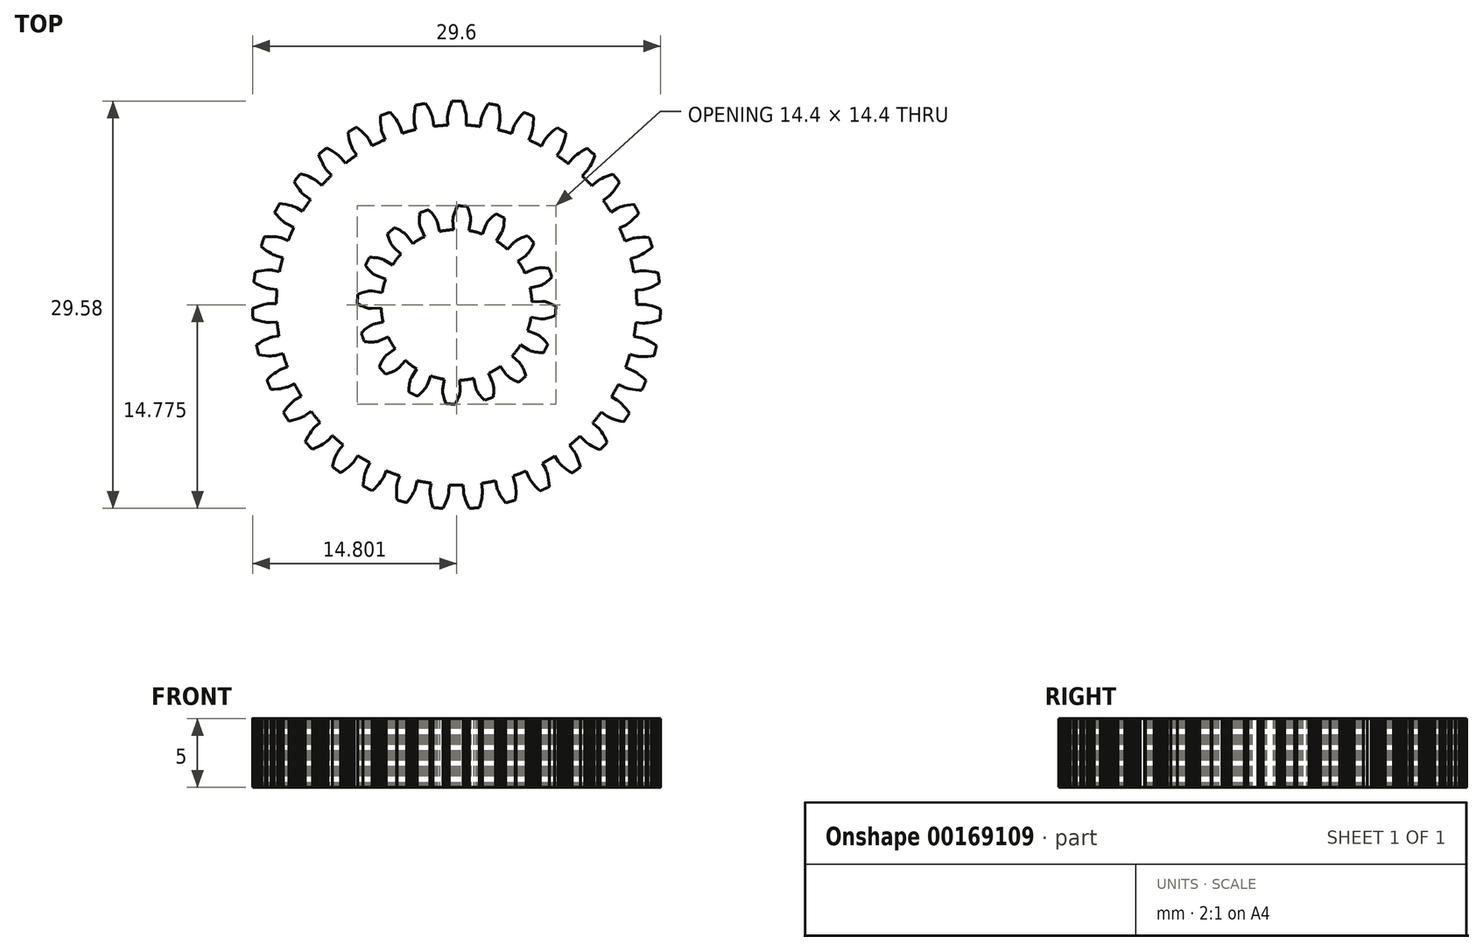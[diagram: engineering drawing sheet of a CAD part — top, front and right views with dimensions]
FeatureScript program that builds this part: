
annotation { "Feature Type Name" : "Feature", "Feature Type Description" : "" }
export const myFeature = defineFeature(function(context is Context, id is Id, definition is map)
    precondition{}
    {
        {
            var Q0;
            Q0=qCreatedBy(makeId("Top.planeOp"),FACE);
            var sketch = newSketch(context, id + "F0", { "sketchPlane" : qUnion([Q0])});
            skLineSegment(sketch, "E0", {"start": v(9.81, 8.62) * mm, "end": v(10.18, 8.94) * mm});
            skLineSegment(sketch, "E1", {"start": v(10.18, 8.94) * mm, "end": v(10.19, 8.95) * mm});
            skLineSegment(sketch, "E2", {"start": v(10.19, 8.95) * mm, "end": v(10.23, 8.98) * mm});
            skLineSegment(sketch, "E3", {"start": v(10.23, 8.98) * mm, "end": v(10.3, 9.03) * mm});
            skLineSegment(sketch, "E4", {"start": v(10.3, 9.03) * mm, "end": v(10.4, 9.1) * mm});
            skLineSegment(sketch, "E5", {"start": v(10.4, 9.1) * mm, "end": v(10.53, 9.16) * mm});
            skLineSegment(sketch, "E6", {"start": v(10.53, 9.16) * mm, "end": v(10.7, 9.24) * mm});
            skLineSegment(sketch, "E7", {"start": v(10.7, 9.24) * mm, "end": v(10.9, 9.33) * mm});
            skLineSegment(sketch, "E8", {"start": v(10.9, 9.33) * mm, "end": v(11.14, 9.41) * mm});
            skLineSegment(sketch, "E9", {"start": v(11.14, 9.41) * mm, "end": v(11.35, 9.48) * mm});
            skArc(sketch, "E10", {"start": v(11.35, 9.48) * mm, "mid": v(11.59, 9.2) * mm, "end": v(11.82, 8.9) * mm});
            skLineSegment(sketch, "E11", {"start": v(11.82, 8.9) * mm, "end": v(11.7, 8.7) * mm});
            skLineSegment(sketch, "E12", {"start": v(11.7, 8.7) * mm, "end": v(11.57, 8.5) * mm});
            skLineSegment(sketch, "E13", {"start": v(11.57, 8.5) * mm, "end": v(11.44, 8.31) * mm});
            skLineSegment(sketch, "E14", {"start": v(11.44, 8.31) * mm, "end": v(11.32, 8.17) * mm});
            skLineSegment(sketch, "E15", {"start": v(11.32, 8.17) * mm, "end": v(11.22, 8.06) * mm});
            skLineSegment(sketch, "E16", {"start": v(11.22, 8.06) * mm, "end": v(11.14, 7.97) * mm});
            skLineSegment(sketch, "E17", {"start": v(11.14, 7.97) * mm, "end": v(11.08, 7.91) * mm});
            skLineSegment(sketch, "E18", {"start": v(11.08, 7.91) * mm, "end": v(11.04, 7.88) * mm});
            skLineSegment(sketch, "E19", {"start": v(11.04, 7.88) * mm, "end": v(11.03, 7.87) * mm});
            skLineSegment(sketch, "E20", {"start": v(11.03, 7.87) * mm, "end": v(10.64, 7.6) * mm});
            skArc(sketch, "E21", {"start": v(10.64, 7.6) * mm, "mid": v(10.93, 7.17) * mm, "end": v(11.2, 6.73) * mm});
            skLineSegment(sketch, "E22", {"start": v(11.2, 6.73) * mm, "end": v(11.61, 6.98) * mm});
            skLineSegment(sketch, "E23", {"start": v(11.61, 6.98) * mm, "end": v(11.63, 6.99) * mm});
            skLineSegment(sketch, "E24", {"start": v(11.63, 6.99) * mm, "end": v(11.67, 7.01) * mm});
            skLineSegment(sketch, "E25", {"start": v(11.67, 7.01) * mm, "end": v(11.75, 7.05) * mm});
            skLineSegment(sketch, "E26", {"start": v(11.75, 7.05) * mm, "end": v(11.86, 7.09) * mm});
            skLineSegment(sketch, "E27", {"start": v(11.86, 7.09) * mm, "end": v(12, 7.13) * mm});
            skLineSegment(sketch, "E28", {"start": v(12, 7.13) * mm, "end": v(12.18, 7.18) * mm});
            skLineSegment(sketch, "E29", {"start": v(12.18, 7.18) * mm, "end": v(12.4, 7.23) * mm});
            skLineSegment(sketch, "E30", {"start": v(12.4, 7.23) * mm, "end": v(12.65, 7.27) * mm});
            skLineSegment(sketch, "E31", {"start": v(12.65, 7.27) * mm, "end": v(12.87, 7.3) * mm});
            skArc(sketch, "E32", {"start": v(12.87, 7.3) * mm, "mid": v(13.05, 6.97) * mm, "end": v(13.22, 6.64) * mm});
            skLineSegment(sketch, "E33", {"start": v(13.22, 6.64) * mm, "end": v(13.08, 6.48) * mm});
            skLineSegment(sketch, "E34", {"start": v(13.08, 6.48) * mm, "end": v(12.9, 6.3) * mm});
            skLineSegment(sketch, "E35", {"start": v(12.9, 6.3) * mm, "end": v(12.74, 6.14) * mm});
            skLineSegment(sketch, "E36", {"start": v(12.74, 6.14) * mm, "end": v(12.6, 6.02) * mm});
            skLineSegment(sketch, "E37", {"start": v(12.6, 6.02) * mm, "end": v(12.48, 5.92) * mm});
            skLineSegment(sketch, "E38", {"start": v(12.48, 5.92) * mm, "end": v(12.39, 5.85) * mm});
            skLineSegment(sketch, "E39", {"start": v(12.39, 5.85) * mm, "end": v(12.32, 5.8) * mm});
            skLineSegment(sketch, "E40", {"start": v(12.32, 5.8) * mm, "end": v(12.27, 5.78) * mm});
            skLineSegment(sketch, "E41", {"start": v(12.27, 5.78) * mm, "end": v(12.26, 5.77) * mm});
            skLineSegment(sketch, "E42", {"start": v(12.26, 5.77) * mm, "end": v(11.82, 5.57) * mm});
            skArc(sketch, "E43", {"start": v(11.82, 5.57) * mm, "mid": v(12.03, 5.1) * mm, "end": v(12.22, 4.62) * mm});
            skLineSegment(sketch, "E44", {"start": v(12.22, 4.62) * mm, "end": v(12.67, 4.8) * mm});
            skLineSegment(sketch, "E45", {"start": v(12.67, 4.8) * mm, "end": v(12.69, 4.8) * mm});
            skLineSegment(sketch, "E46", {"start": v(12.69, 4.8) * mm, "end": v(12.74, 4.81) * mm});
            skLineSegment(sketch, "E47", {"start": v(12.74, 4.81) * mm, "end": v(12.82, 4.83) * mm});
            skLineSegment(sketch, "E48", {"start": v(12.82, 4.83) * mm, "end": v(12.94, 4.86) * mm});
            skLineSegment(sketch, "E49", {"start": v(12.94, 4.86) * mm, "end": v(13.09, 4.88) * mm});
            skLineSegment(sketch, "E50", {"start": v(13.09, 4.88) * mm, "end": v(13.27, 4.9) * mm});
            skLineSegment(sketch, "E51", {"start": v(13.27, 4.9) * mm, "end": v(13.5, 4.9) * mm});
            skLineSegment(sketch, "E52", {"start": v(13.5, 4.9) * mm, "end": v(13.75, 4.9) * mm});
            skLineSegment(sketch, "E53", {"start": v(13.75, 4.9) * mm, "end": v(13.97, 4.88) * mm});
            skArc(sketch, "E54", {"start": v(13.97, 4.88) * mm, "mid": v(14.09, 4.53) * mm, "end": v(14.2, 4.18) * mm});
            skLineSegment(sketch, "E55", {"start": v(14.2, 4.18) * mm, "end": v(14.03, 4.04) * mm});
            skLineSegment(sketch, "E56", {"start": v(14.03, 4.04) * mm, "end": v(13.82, 3.89) * mm});
            skLineSegment(sketch, "E57", {"start": v(13.82, 3.89) * mm, "end": v(13.64, 3.76) * mm});
            skLineSegment(sketch, "E58", {"start": v(13.64, 3.76) * mm, "end": v(13.48, 3.67) * mm});
            skLineSegment(sketch, "E59", {"start": v(13.48, 3.67) * mm, "end": v(13.34, 3.6) * mm});
            skLineSegment(sketch, "E60", {"start": v(13.34, 3.6) * mm, "end": v(13.24, 3.55) * mm});
            skLineSegment(sketch, "E61", {"start": v(13.24, 3.55) * mm, "end": v(13.16, 3.51) * mm});
            skLineSegment(sketch, "E62", {"start": v(13.16, 3.51) * mm, "end": v(13.1, 3.5) * mm});
            skLineSegment(sketch, "E63", {"start": v(13.1, 3.5) * mm, "end": v(13.1, 3.5) * mm});
            skLineSegment(sketch, "E64", {"start": v(13.1, 3.5) * mm, "end": v(12.63, 3.37) * mm});
            skArc(sketch, "E65", {"start": v(12.63, 3.37) * mm, "mid": v(12.75, 2.87) * mm, "end": v(12.86, 2.37) * mm});
            skLineSegment(sketch, "E66", {"start": v(12.86, 2.37) * mm, "end": v(13.33, 2.45) * mm});
            skLineSegment(sketch, "E67", {"start": v(13.33, 2.45) * mm, "end": v(13.34, 2.46) * mm});
            skLineSegment(sketch, "E68", {"start": v(13.34, 2.46) * mm, "end": v(13.4, 2.46) * mm});
            skLineSegment(sketch, "E69", {"start": v(13.4, 2.46) * mm, "end": v(13.48, 2.47) * mm});
            skLineSegment(sketch, "E70", {"start": v(13.48, 2.47) * mm, "end": v(13.6, 2.47) * mm});
            skLineSegment(sketch, "E71", {"start": v(13.6, 2.47) * mm, "end": v(13.75, 2.46) * mm});
            skLineSegment(sketch, "E72", {"start": v(13.75, 2.46) * mm, "end": v(13.94, 2.44) * mm});
            skLineSegment(sketch, "E73", {"start": v(13.94, 2.44) * mm, "end": v(14.15, 2.41) * mm});
            skLineSegment(sketch, "E74", {"start": v(14.15, 2.41) * mm, "end": v(14.4, 2.36) * mm});
            skLineSegment(sketch, "E75", {"start": v(14.4, 2.36) * mm, "end": v(14.62, 2.31) * mm});
            skArc(sketch, "E76", {"start": v(14.62, 2.31) * mm, "mid": v(14.67, 1.94) * mm, "end": v(14.71, 1.57) * mm});
            skLineSegment(sketch, "E77", {"start": v(14.71, 1.57) * mm, "end": v(14.52, 1.47) * mm});
            skLineSegment(sketch, "E78", {"start": v(14.52, 1.47) * mm, "end": v(14.3, 1.36) * mm});
            skLineSegment(sketch, "E79", {"start": v(14.3, 1.36) * mm, "end": v(14.1, 1.27) * mm});
            skLineSegment(sketch, "E80", {"start": v(14.1, 1.27) * mm, "end": v(13.92, 1.2) * mm});
            skLineSegment(sketch, "E81", {"start": v(13.92, 1.2) * mm, "end": v(13.77, 1.16) * mm});
            skLineSegment(sketch, "E82", {"start": v(13.77, 1.16) * mm, "end": v(13.66, 1.13) * mm});
            skLineSegment(sketch, "E83", {"start": v(13.66, 1.13) * mm, "end": v(13.58, 1.1) * mm});
            skLineSegment(sketch, "E84", {"start": v(13.58, 1.1) * mm, "end": v(13.53, 1.1) * mm});
            skLineSegment(sketch, "E85", {"start": v(13.53, 1.1) * mm, "end": v(13.5, 1.1) * mm});
            skLineSegment(sketch, "E86", {"start": v(13.5, 1.1) * mm, "end": v(13.03, 1.06) * mm});
            skArc(sketch, "E87", {"start": v(13.03, 1.06) * mm, "mid": v(13.06, 0.55) * mm, "end": v(13.07, 0.03) * mm});
            skLineSegment(sketch, "E88", {"start": v(13.07, 0.03) * mm, "end": v(13.55, 0.04) * mm});
            skLineSegment(sketch, "E89", {"start": v(13.55, 0.04) * mm, "end": v(13.57, 0.03) * mm});
            skLineSegment(sketch, "E90", {"start": v(13.57, 0.03) * mm, "end": v(13.62, 0.03) * mm});
            skLineSegment(sketch, "E91", {"start": v(13.62, 0.03) * mm, "end": v(13.7, 0.02) * mm});
            skLineSegment(sketch, "E92", {"start": v(13.7, 0.02) * mm, "end": v(13.82, 0) * mm});
            skLineSegment(sketch, "E93", {"start": v(13.82, 0) * mm, "end": v(13.97, -0.03) * mm});
            skLineSegment(sketch, "E94", {"start": v(13.97, -0.03) * mm, "end": v(14.15, -0.08) * mm});
            skLineSegment(sketch, "E95", {"start": v(14.15, -0.08) * mm, "end": v(14.36, -0.15) * mm});
            skLineSegment(sketch, "E96", {"start": v(14.36, -0.15) * mm, "end": v(14.6, -0.25) * mm});
            skLineSegment(sketch, "E97", {"start": v(14.6, -0.25) * mm, "end": v(14.8, -0.34) * mm});
            skArc(sketch, "E98", {"start": v(14.8, -0.34) * mm, "mid": v(14.78, -0.7) * mm, "end": v(14.76, -1.08) * mm});
            skLineSegment(sketch, "E99", {"start": v(14.76, -1.08) * mm, "end": v(14.55, -1.15) * mm});
            skLineSegment(sketch, "E100", {"start": v(14.55, -1.15) * mm, "end": v(14.31, -1.22) * mm});
            skLineSegment(sketch, "E101", {"start": v(14.31, -1.22) * mm, "end": v(14.1, -1.27) * mm});
            skLineSegment(sketch, "E102", {"start": v(14.1, -1.27) * mm, "end": v(13.91, -1.3) * mm});
            skLineSegment(sketch, "E103", {"start": v(13.91, -1.3) * mm, "end": v(13.76, -1.32) * mm});
            skLineSegment(sketch, "E104", {"start": v(13.76, -1.32) * mm, "end": v(13.64, -1.33) * mm});
            skLineSegment(sketch, "E105", {"start": v(13.64, -1.33) * mm, "end": v(13.56, -1.33) * mm});
            skLineSegment(sketch, "E106", {"start": v(13.56, -1.33) * mm, "end": v(13.5, -1.33) * mm});
            skLineSegment(sketch, "E107", {"start": v(13.5, -1.33) * mm, "end": v(13.5, -1.33) * mm});
            skLineSegment(sketch, "E108", {"start": v(13.5, -1.33) * mm, "end": v(13.01, -1.28) * mm});
            skArc(sketch, "E109", {"start": v(13.01, -1.28) * mm, "mid": v(12.95, -1.8) * mm, "end": v(12.87, -2.3) * mm});
            skLineSegment(sketch, "E110", {"start": v(12.87, -2.3) * mm, "end": v(13.35, -2.39) * mm});
            skLineSegment(sketch, "E111", {"start": v(13.35, -2.39) * mm, "end": v(13.36, -2.39) * mm});
            skLineSegment(sketch, "E112", {"start": v(13.36, -2.39) * mm, "end": v(13.41, -2.4) * mm});
            skLineSegment(sketch, "E113", {"start": v(13.41, -2.4) * mm, "end": v(13.5, -2.43) * mm});
            skLineSegment(sketch, "E114", {"start": v(13.5, -2.43) * mm, "end": v(13.6, -2.47) * mm});
            skLineSegment(sketch, "E115", {"start": v(13.6, -2.47) * mm, "end": v(13.74, -2.53) * mm});
            skLineSegment(sketch, "E116", {"start": v(13.74, -2.53) * mm, "end": v(13.91, -2.6) * mm});
            skLineSegment(sketch, "E117", {"start": v(13.91, -2.6) * mm, "end": v(14.1, -2.72) * mm});
            skLineSegment(sketch, "E118", {"start": v(14.1, -2.72) * mm, "end": v(14.32, -2.85) * mm});
            skLineSegment(sketch, "E119", {"start": v(14.32, -2.85) * mm, "end": v(14.5, -2.97) * mm});
            skArc(sketch, "E120", {"start": v(14.5, -2.97) * mm, "mid": v(14.42, -3.34) * mm, "end": v(14.34, -3.7) * mm});
            skLineSegment(sketch, "E121", {"start": v(14.34, -3.7) * mm, "end": v(14.12, -3.73) * mm});
            skLineSegment(sketch, "E122", {"start": v(14.12, -3.73) * mm, "end": v(13.87, -3.75) * mm});
            skLineSegment(sketch, "E123", {"start": v(13.87, -3.75) * mm, "end": v(13.65, -3.77) * mm});
            skLineSegment(sketch, "E124", {"start": v(13.65, -3.77) * mm, "end": v(13.46, -3.77) * mm});
            skLineSegment(sketch, "E125", {"start": v(13.46, -3.77) * mm, "end": v(13.3, -3.76) * mm});
            skLineSegment(sketch, "E126", {"start": v(13.3, -3.76) * mm, "end": v(13.19, -3.75) * mm});
            skLineSegment(sketch, "E127", {"start": v(13.19, -3.75) * mm, "end": v(13.1, -3.73) * mm});
            skLineSegment(sketch, "E128", {"start": v(13.1, -3.73) * mm, "end": v(13.06, -3.72) * mm});
            skLineSegment(sketch, "E129", {"start": v(13.06, -3.72) * mm, "end": v(13.04, -3.72) * mm});
            skLineSegment(sketch, "E130", {"start": v(13.04, -3.72) * mm, "end": v(12.58, -3.59) * mm});
            skArc(sketch, "E131", {"start": v(12.58, -3.59) * mm, "mid": v(12.43, -4.08) * mm, "end": v(12.26, -4.56) * mm});
            skLineSegment(sketch, "E132", {"start": v(12.26, -4.56) * mm, "end": v(12.7, -4.73) * mm});
            skLineSegment(sketch, "E133", {"start": v(12.7, -4.73) * mm, "end": v(12.72, -4.74) * mm});
            skLineSegment(sketch, "E134", {"start": v(12.72, -4.74) * mm, "end": v(12.77, -4.76) * mm});
            skLineSegment(sketch, "E135", {"start": v(12.77, -4.76) * mm, "end": v(12.84, -4.8) * mm});
            skLineSegment(sketch, "E136", {"start": v(12.84, -4.8) * mm, "end": v(12.95, -4.86) * mm});
            skLineSegment(sketch, "E137", {"start": v(12.95, -4.86) * mm, "end": v(13.07, -4.94) * mm});
            skLineSegment(sketch, "E138", {"start": v(13.07, -4.94) * mm, "end": v(13.22, -5.05) * mm});
            skLineSegment(sketch, "E139", {"start": v(13.22, -5.05) * mm, "end": v(13.4, -5.2) * mm});
            skLineSegment(sketch, "E140", {"start": v(13.4, -5.2) * mm, "end": v(13.58, -5.36) * mm});
            skLineSegment(sketch, "E141", {"start": v(13.58, -5.36) * mm, "end": v(13.74, -5.51) * mm});
            skArc(sketch, "E142", {"start": v(13.74, -5.51) * mm, "mid": v(13.6, -5.86) * mm, "end": v(13.45, -6.2) * mm});
            skLineSegment(sketch, "E143", {"start": v(13.45, -6.2) * mm, "end": v(13.23, -6.2) * mm});
            skLineSegment(sketch, "E144", {"start": v(13.23, -6.2) * mm, "end": v(12.97, -6.17) * mm});
            skLineSegment(sketch, "E145", {"start": v(12.97, -6.17) * mm, "end": v(12.76, -6.14) * mm});
            skLineSegment(sketch, "E146", {"start": v(12.76, -6.14) * mm, "end": v(12.57, -6.1) * mm});
            skLineSegment(sketch, "E147", {"start": v(12.57, -6.1) * mm, "end": v(12.42, -6.07) * mm});
            skLineSegment(sketch, "E148", {"start": v(12.42, -6.07) * mm, "end": v(12.31, -6.04) * mm});
            skLineSegment(sketch, "E149", {"start": v(12.31, -6.04) * mm, "end": v(12.23, -6.01) * mm});
            skLineSegment(sketch, "E150", {"start": v(12.23, -6.01) * mm, "end": v(12.18, -6) * mm});
            skLineSegment(sketch, "E151", {"start": v(12.18, -6) * mm, "end": v(12.17, -5.99) * mm});
            skLineSegment(sketch, "E152", {"start": v(12.17, -5.99) * mm, "end": v(11.74, -5.78) * mm});
            skArc(sketch, "E153", {"start": v(11.74, -5.78) * mm, "mid": v(11.5, -6.23) * mm, "end": v(11.25, -6.68) * mm});
            skLineSegment(sketch, "E154", {"start": v(11.25, -6.68) * mm, "end": v(11.66, -6.92) * mm});
            skLineSegment(sketch, "E155", {"start": v(11.66, -6.92) * mm, "end": v(11.68, -6.93) * mm});
            skLineSegment(sketch, "E156", {"start": v(11.68, -6.93) * mm, "end": v(11.72, -6.96) * mm});
            skLineSegment(sketch, "E157", {"start": v(11.72, -6.96) * mm, "end": v(11.78, -7.01) * mm});
            skLineSegment(sketch, "E158", {"start": v(11.78, -7.01) * mm, "end": v(11.87, -7.1) * mm});
            skLineSegment(sketch, "E159", {"start": v(11.87, -7.1) * mm, "end": v(11.98, -7.2) * mm});
            skLineSegment(sketch, "E160", {"start": v(11.98, -7.2) * mm, "end": v(12.11, -7.33) * mm});
            skLineSegment(sketch, "E161", {"start": v(12.11, -7.33) * mm, "end": v(12.26, -7.5) * mm});
            skLineSegment(sketch, "E162", {"start": v(12.26, -7.5) * mm, "end": v(12.41, -7.7) * mm});
            skLineSegment(sketch, "E163", {"start": v(12.41, -7.7) * mm, "end": v(12.54, -7.88) * mm});
            skArc(sketch, "E164", {"start": v(12.54, -7.88) * mm, "mid": v(12.34, -8.2) * mm, "end": v(12.13, -8.5) * mm});
            skLineSegment(sketch, "E165", {"start": v(12.13, -8.5) * mm, "end": v(11.91, -8.45) * mm});
            skLineSegment(sketch, "E166", {"start": v(11.91, -8.45) * mm, "end": v(11.67, -8.39) * mm});
            skLineSegment(sketch, "E167", {"start": v(11.67, -8.39) * mm, "end": v(11.46, -8.32) * mm});
            skLineSegment(sketch, "E168", {"start": v(11.46, -8.32) * mm, "end": v(11.28, -8.25) * mm});
            skLineSegment(sketch, "E169", {"start": v(11.28, -8.25) * mm, "end": v(11.14, -8.2) * mm});
            skLineSegment(sketch, "E170", {"start": v(11.14, -8.2) * mm, "end": v(11.04, -8.14) * mm});
            skLineSegment(sketch, "E171", {"start": v(11.04, -8.14) * mm, "end": v(10.96, -8.1) * mm});
            skLineSegment(sketch, "E172", {"start": v(10.96, -8.1) * mm, "end": v(10.92, -8.07) * mm});
            skLineSegment(sketch, "E173", {"start": v(10.92, -8.07) * mm, "end": v(10.9, -8.06) * mm});
            skLineSegment(sketch, "E174", {"start": v(10.9, -8.06) * mm, "end": v(10.52, -7.78) * mm});
            skArc(sketch, "E175", {"start": v(10.52, -7.78) * mm, "mid": v(10.2, -8.19) * mm, "end": v(9.88, -8.58) * mm});
            skLineSegment(sketch, "E176", {"start": v(9.88, -8.58) * mm, "end": v(10.24, -8.9) * mm});
            skLineSegment(sketch, "E177", {"start": v(10.24, -8.9) * mm, "end": v(10.25, -8.9) * mm});
            skLineSegment(sketch, "E178", {"start": v(10.25, -8.9) * mm, "end": v(10.29, -8.94) * mm});
            skLineSegment(sketch, "E179", {"start": v(10.29, -8.94) * mm, "end": v(10.34, -9) * mm});
            skLineSegment(sketch, "E180", {"start": v(10.34, -9) * mm, "end": v(10.42, -9.1) * mm});
            skLineSegment(sketch, "E181", {"start": v(10.42, -9.1) * mm, "end": v(10.5, -9.22) * mm});
            skLineSegment(sketch, "E182", {"start": v(10.5, -9.22) * mm, "end": v(10.61, -9.38) * mm});
            skLineSegment(sketch, "E183", {"start": v(10.61, -9.38) * mm, "end": v(10.72, -9.57) * mm});
            skLineSegment(sketch, "E184", {"start": v(10.72, -9.57) * mm, "end": v(10.84, -9.8) * mm});
            skLineSegment(sketch, "E185", {"start": v(10.84, -9.8) * mm, "end": v(10.93, -10) * mm});
            skArc(sketch, "E186", {"start": v(10.93, -10) * mm, "mid": v(10.68, -10.26) * mm, "end": v(10.42, -10.53) * mm});
            skLineSegment(sketch, "E187", {"start": v(10.42, -10.53) * mm, "end": v(10.21, -10.44) * mm});
            skLineSegment(sketch, "E188", {"start": v(10.21, -10.44) * mm, "end": v(9.98, -10.34) * mm});
            skLineSegment(sketch, "E189", {"start": v(9.98, -10.34) * mm, "end": v(9.8, -10.23) * mm});
            skLineSegment(sketch, "E190", {"start": v(9.8, -10.23) * mm, "end": v(9.63, -10.14) * mm});
            skLineSegment(sketch, "E191", {"start": v(9.63, -10.14) * mm, "end": v(9.5, -10.05) * mm});
            skLineSegment(sketch, "E192", {"start": v(9.5, -10.05) * mm, "end": v(9.4, -9.98) * mm});
            skLineSegment(sketch, "E193", {"start": v(9.4, -9.98) * mm, "end": v(9.34, -9.93) * mm});
            skLineSegment(sketch, "E194", {"start": v(9.34, -9.93) * mm, "end": v(9.3, -9.9) * mm});
            skLineSegment(sketch, "E195", {"start": v(9.3, -9.9) * mm, "end": v(9.3, -9.88) * mm});
            skLineSegment(sketch, "E196", {"start": v(9.3, -9.88) * mm, "end": v(8.96, -9.53) * mm});
            skArc(sketch, "E197", {"start": v(8.96, -9.53) * mm, "mid": v(8.58, -9.88) * mm, "end": v(8.19, -10.2) * mm});
            skLineSegment(sketch, "E198", {"start": v(8.19, -10.2) * mm, "end": v(8.5, -10.58) * mm});
            skLineSegment(sketch, "E199", {"start": v(8.5, -10.58) * mm, "end": v(8.5, -10.6) * mm});
            skLineSegment(sketch, "E200", {"start": v(8.5, -10.6) * mm, "end": v(8.53, -10.64) * mm});
            skLineSegment(sketch, "E201", {"start": v(8.53, -10.64) * mm, "end": v(8.57, -10.7) * mm});
            skLineSegment(sketch, "E202", {"start": v(8.57, -10.7) * mm, "end": v(8.63, -10.81) * mm});
            skLineSegment(sketch, "E203", {"start": v(8.63, -10.81) * mm, "end": v(8.7, -10.95) * mm});
            skLineSegment(sketch, "E204", {"start": v(8.7, -10.95) * mm, "end": v(8.77, -11.12) * mm});
            skLineSegment(sketch, "E205", {"start": v(8.77, -11.12) * mm, "end": v(8.85, -11.33) * mm});
            skLineSegment(sketch, "E206", {"start": v(8.85, -11.33) * mm, "end": v(8.92, -11.57) * mm});
            skLineSegment(sketch, "E207", {"start": v(8.92, -11.57) * mm, "end": v(8.98, -11.78) * mm});
            skArc(sketch, "E208", {"start": v(8.98, -11.78) * mm, "mid": v(8.68, -12) * mm, "end": v(8.37, -12.22) * mm});
            skLineSegment(sketch, "E209", {"start": v(8.37, -12.22) * mm, "end": v(8.19, -12.1) * mm});
            skLineSegment(sketch, "E210", {"start": v(8.19, -12.1) * mm, "end": v(7.98, -11.95) * mm});
            skLineSegment(sketch, "E211", {"start": v(7.98, -11.95) * mm, "end": v(7.8, -11.82) * mm});
            skLineSegment(sketch, "E212", {"start": v(7.8, -11.82) * mm, "end": v(7.67, -11.7) * mm});
            skLineSegment(sketch, "E213", {"start": v(7.67, -11.7) * mm, "end": v(7.56, -11.59) * mm});
            skLineSegment(sketch, "E214", {"start": v(7.56, -11.59) * mm, "end": v(7.48, -11.5) * mm});
            skLineSegment(sketch, "E215", {"start": v(7.48, -11.5) * mm, "end": v(7.42, -11.44) * mm});
            skLineSegment(sketch, "E216", {"start": v(7.42, -11.44) * mm, "end": v(7.4, -11.4) * mm});
            skLineSegment(sketch, "E217", {"start": v(7.4, -11.4) * mm, "end": v(7.38, -11.38) * mm});
            skLineSegment(sketch, "E218", {"start": v(7.38, -11.38) * mm, "end": v(7.12, -10.98) * mm});
            skArc(sketch, "E219", {"start": v(7.12, -10.98) * mm, "mid": v(6.68, -11.25) * mm, "end": v(6.24, -11.5) * mm});
            skLineSegment(sketch, "E220", {"start": v(6.24, -11.5) * mm, "end": v(6.47, -11.93) * mm});
            skLineSegment(sketch, "E221", {"start": v(6.47, -11.93) * mm, "end": v(6.47, -11.94) * mm});
            skLineSegment(sketch, "E222", {"start": v(6.47, -11.94) * mm, "end": v(6.5, -11.99) * mm});
            skLineSegment(sketch, "E223", {"start": v(6.5, -11.99) * mm, "end": v(6.53, -12.07) * mm});
            skLineSegment(sketch, "E224", {"start": v(6.53, -12.07) * mm, "end": v(6.56, -12.18) * mm});
            skLineSegment(sketch, "E225", {"start": v(6.56, -12.18) * mm, "end": v(6.6, -12.33) * mm});
            skLineSegment(sketch, "E226", {"start": v(6.6, -12.33) * mm, "end": v(6.65, -12.5) * mm});
            skLineSegment(sketch, "E227", {"start": v(6.65, -12.5) * mm, "end": v(6.68, -12.73) * mm});
            skLineSegment(sketch, "E228", {"start": v(6.68, -12.73) * mm, "end": v(6.71, -12.98) * mm});
            skLineSegment(sketch, "E229", {"start": v(6.71, -12.98) * mm, "end": v(6.73, -13.2) * mm});
            skArc(sketch, "E230", {"start": v(6.73, -13.2) * mm, "mid": v(6.4, -13.36) * mm, "end": v(6.06, -13.52) * mm});
            skLineSegment(sketch, "E231", {"start": v(6.06, -13.52) * mm, "end": v(5.9, -13.37) * mm});
            skLineSegment(sketch, "E232", {"start": v(5.9, -13.37) * mm, "end": v(5.72, -13.19) * mm});
            skLineSegment(sketch, "E233", {"start": v(5.72, -13.19) * mm, "end": v(5.58, -13.02) * mm});
            skLineSegment(sketch, "E234", {"start": v(5.58, -13.02) * mm, "end": v(5.46, -12.88) * mm});
            skLineSegment(sketch, "E235", {"start": v(5.46, -12.88) * mm, "end": v(5.37, -12.75) * mm});
            skLineSegment(sketch, "E236", {"start": v(5.37, -12.75) * mm, "end": v(5.3, -12.65) * mm});
            skLineSegment(sketch, "E237", {"start": v(5.3, -12.65) * mm, "end": v(5.26, -12.58) * mm});
            skLineSegment(sketch, "E238", {"start": v(5.26, -12.58) * mm, "end": v(5.24, -12.53) * mm});
            skLineSegment(sketch, "E239", {"start": v(5.24, -12.53) * mm, "end": v(5.23, -12.52) * mm});
            skLineSegment(sketch, "E240", {"start": v(5.23, -12.52) * mm, "end": v(5.05, -12.08) * mm});
            skArc(sketch, "E241", {"start": v(5.05, -12.08) * mm, "mid": v(4.57, -12.26) * mm, "end": v(4.09, -12.43) * mm});
            skLineSegment(sketch, "E242", {"start": v(4.09, -12.43) * mm, "end": v(4.24, -12.89) * mm});
            skLineSegment(sketch, "E243", {"start": v(4.24, -12.89) * mm, "end": v(4.24, -12.9) * mm});
            skLineSegment(sketch, "E244", {"start": v(4.24, -12.9) * mm, "end": v(4.25, -12.96) * mm});
            skLineSegment(sketch, "E245", {"start": v(4.25, -12.96) * mm, "end": v(4.27, -13.04) * mm});
            skLineSegment(sketch, "E246", {"start": v(4.27, -13.04) * mm, "end": v(4.29, -13.16) * mm});
            skLineSegment(sketch, "E247", {"start": v(4.29, -13.16) * mm, "end": v(4.3, -13.3) * mm});
            skLineSegment(sketch, "E248", {"start": v(4.3, -13.3) * mm, "end": v(4.3, -13.5) * mm});
            skLineSegment(sketch, "E249", {"start": v(4.3, -13.5) * mm, "end": v(4.3, -13.71) * mm});
            skLineSegment(sketch, "E250", {"start": v(4.3, -13.71) * mm, "end": v(4.3, -13.97) * mm});
            skLineSegment(sketch, "E251", {"start": v(4.3, -13.97) * mm, "end": v(4.27, -14.19) * mm});
            skArc(sketch, "E252", {"start": v(4.27, -14.19) * mm, "mid": v(3.91, -14.29) * mm, "end": v(3.55, -14.38) * mm});
            skLineSegment(sketch, "E253", {"start": v(3.55, -14.38) * mm, "end": v(3.42, -14.2) * mm});
            skLineSegment(sketch, "E254", {"start": v(3.42, -14.2) * mm, "end": v(3.28, -14) * mm});
            skLineSegment(sketch, "E255", {"start": v(3.28, -14) * mm, "end": v(3.16, -13.8) * mm});
            skLineSegment(sketch, "E256", {"start": v(3.16, -13.8) * mm, "end": v(3.08, -13.64) * mm});
            skLineSegment(sketch, "E257", {"start": v(3.08, -13.64) * mm, "end": v(3.01, -13.5) * mm});
            skLineSegment(sketch, "E258", {"start": v(3.01, -13.5) * mm, "end": v(2.96, -13.4) * mm});
            skLineSegment(sketch, "E259", {"start": v(2.96, -13.4) * mm, "end": v(2.94, -13.32) * mm});
            skLineSegment(sketch, "E260", {"start": v(2.94, -13.32) * mm, "end": v(2.92, -13.27) * mm});
            skLineSegment(sketch, "E261", {"start": v(2.92, -13.27) * mm, "end": v(2.92, -13.25) * mm});
            skLineSegment(sketch, "E262", {"start": v(2.92, -13.25) * mm, "end": v(2.81, -12.78) * mm});
            skArc(sketch, "E263", {"start": v(2.81, -12.78) * mm, "mid": v(2.31, -12.88) * mm, "end": v(1.8, -12.96) * mm});
            skLineSegment(sketch, "E264", {"start": v(1.8, -12.96) * mm, "end": v(1.87, -13.44) * mm});
            skLineSegment(sketch, "E265", {"start": v(1.87, -13.44) * mm, "end": v(1.87, -13.46) * mm});
            skLineSegment(sketch, "E266", {"start": v(1.87, -13.46) * mm, "end": v(1.87, -13.5) * mm});
            skLineSegment(sketch, "E267", {"start": v(1.87, -13.5) * mm, "end": v(1.87, -13.6) * mm});
            skLineSegment(sketch, "E268", {"start": v(1.87, -13.6) * mm, "end": v(1.87, -13.7) * mm});
            skLineSegment(sketch, "E269", {"start": v(1.87, -13.7) * mm, "end": v(1.86, -13.86) * mm});
            skLineSegment(sketch, "E270", {"start": v(1.86, -13.86) * mm, "end": v(1.83, -14.05) * mm});
            skLineSegment(sketch, "E271", {"start": v(1.83, -14.05) * mm, "end": v(1.8, -14.26) * mm});
            skLineSegment(sketch, "E272", {"start": v(1.8, -14.26) * mm, "end": v(1.73, -14.5) * mm});
            skLineSegment(sketch, "E273", {"start": v(1.73, -14.5) * mm, "end": v(1.67, -14.72) * mm});
            skArc(sketch, "E274", {"start": v(1.67, -14.72) * mm, "mid": v(1.3, -14.76) * mm, "end": v(0.93, -14.79) * mm});
            skLineSegment(sketch, "E275", {"start": v(0.93, -14.79) * mm, "end": v(0.83, -14.59) * mm});
            skLineSegment(sketch, "E276", {"start": v(0.83, -14.59) * mm, "end": v(0.73, -14.36) * mm});
            skLineSegment(sketch, "E277", {"start": v(0.73, -14.36) * mm, "end": v(0.65, -14.15) * mm});
            skLineSegment(sketch, "E278", {"start": v(0.65, -14.15) * mm, "end": v(0.6, -13.97) * mm});
            skLineSegment(sketch, "E279", {"start": v(0.6, -13.97) * mm, "end": v(0.55, -13.83) * mm});
            skLineSegment(sketch, "E280", {"start": v(0.55, -13.83) * mm, "end": v(0.53, -13.71) * mm});
            skLineSegment(sketch, "E281", {"start": v(0.53, -13.71) * mm, "end": v(0.51, -13.63) * mm});
            skLineSegment(sketch, "E282", {"start": v(0.51, -13.63) * mm, "end": v(0.5, -13.58) * mm});
            skLineSegment(sketch, "E283", {"start": v(0.5, -13.58) * mm, "end": v(0.5, -13.56) * mm});
            skLineSegment(sketch, "E284", {"start": v(0.5, -13.56) * mm, "end": v(0.49, -13.08) * mm});
            skArc(sketch, "E285", {"start": v(0.49, -13.08) * mm, "mid": v(-0.02, -13.09) * mm, "end": v(-0.54, -13.08) * mm});
            skLineSegment(sketch, "E286", {"start": v(-0.54, -13.08) * mm, "end": v(-0.56, -13.56) * mm});
            skLineSegment(sketch, "E287", {"start": v(-0.56, -13.56) * mm, "end": v(-0.56, -13.57) * mm});
            skLineSegment(sketch, "E288", {"start": v(-0.56, -13.57) * mm, "end": v(-0.57, -13.62) * mm});
            skLineSegment(sketch, "E289", {"start": v(-0.57, -13.62) * mm, "end": v(-0.58, -13.7) * mm});
            skLineSegment(sketch, "E290", {"start": v(-0.58, -13.7) * mm, "end": v(-0.6, -13.82) * mm});
            skLineSegment(sketch, "E291", {"start": v(-0.6, -13.82) * mm, "end": v(-0.65, -13.97) * mm});
            skLineSegment(sketch, "E292", {"start": v(-0.65, -13.97) * mm, "end": v(-0.7, -14.15) * mm});
            skLineSegment(sketch, "E293", {"start": v(-0.7, -14.15) * mm, "end": v(-0.78, -14.35) * mm});
            skLineSegment(sketch, "E294", {"start": v(-0.78, -14.35) * mm, "end": v(-0.89, -14.59) * mm});
            skLineSegment(sketch, "E295", {"start": v(-0.89, -14.59) * mm, "end": v(-0.98, -14.78) * mm});
            skArc(sketch, "E296", {"start": v(-0.98, -14.78) * mm, "mid": v(-1.35, -14.75) * mm, "end": v(-1.72, -14.71) * mm});
            skLineSegment(sketch, "E297", {"start": v(-1.72, -14.71) * mm, "end": v(-1.79, -14.5) * mm});
            skLineSegment(sketch, "E298", {"start": v(-1.79, -14.5) * mm, "end": v(-1.84, -14.26) * mm});
            skLineSegment(sketch, "E299", {"start": v(-1.84, -14.26) * mm, "end": v(-1.88, -14.04) * mm});
            skLineSegment(sketch, "E300", {"start": v(-1.88, -14.04) * mm, "end": v(-1.9, -13.85) * mm});
            skLineSegment(sketch, "E301", {"start": v(-1.9, -13.85) * mm, "end": v(-1.92, -13.7) * mm});
            skLineSegment(sketch, "E302", {"start": v(-1.92, -13.7) * mm, "end": v(-1.93, -13.58) * mm});
            skLineSegment(sketch, "E303", {"start": v(-1.93, -13.58) * mm, "end": v(-1.92, -13.5) * mm});
            skLineSegment(sketch, "E304", {"start": v(-1.92, -13.5) * mm, "end": v(-1.92, -13.45) * mm});
            skLineSegment(sketch, "E305", {"start": v(-1.92, -13.45) * mm, "end": v(-1.92, -13.43) * mm});
            skLineSegment(sketch, "E306", {"start": v(-1.92, -13.43) * mm, "end": v(-1.85, -12.96) * mm});
            skArc(sketch, "E307", {"start": v(-1.85, -12.96) * mm, "mid": v(-2.36, -12.87) * mm, "end": v(-2.86, -12.77) * mm});
            skLineSegment(sketch, "E308", {"start": v(-2.86, -12.77) * mm, "end": v(-2.97, -13.24) * mm});
            skLineSegment(sketch, "E309", {"start": v(-2.97, -13.24) * mm, "end": v(-2.97, -13.26) * mm});
            skLineSegment(sketch, "E310", {"start": v(-2.97, -13.26) * mm, "end": v(-2.99, -13.3) * mm});
            skLineSegment(sketch, "E311", {"start": v(-2.99, -13.3) * mm, "end": v(-3.02, -13.38) * mm});
            skLineSegment(sketch, "E312", {"start": v(-3.02, -13.38) * mm, "end": v(-3.06, -13.5) * mm});
            skLineSegment(sketch, "E313", {"start": v(-3.06, -13.5) * mm, "end": v(-3.13, -13.63) * mm});
            skLineSegment(sketch, "E314", {"start": v(-3.13, -13.63) * mm, "end": v(-3.22, -13.8) * mm});
            skLineSegment(sketch, "E315", {"start": v(-3.22, -13.8) * mm, "end": v(-3.33, -13.98) * mm});
            skLineSegment(sketch, "E316", {"start": v(-3.33, -13.98) * mm, "end": v(-3.47, -14.2) * mm});
            skLineSegment(sketch, "E317", {"start": v(-3.47, -14.2) * mm, "end": v(-3.6, -14.37) * mm});
            skArc(sketch, "E318", {"start": v(-3.6, -14.37) * mm, "mid": v(-3.96, -14.27) * mm, "end": v(-4.32, -14.17) * mm});
            skLineSegment(sketch, "E319", {"start": v(-4.32, -14.17) * mm, "end": v(-4.34, -13.95) * mm});
            skLineSegment(sketch, "E320", {"start": v(-4.34, -13.95) * mm, "end": v(-4.36, -13.7) * mm});
            skLineSegment(sketch, "E321", {"start": v(-4.36, -13.7) * mm, "end": v(-4.36, -13.48) * mm});
            skLineSegment(sketch, "E322", {"start": v(-4.36, -13.48) * mm, "end": v(-4.35, -13.3) * mm});
            skLineSegment(sketch, "E323", {"start": v(-4.35, -13.3) * mm, "end": v(-4.34, -13.14) * mm});
            skLineSegment(sketch, "E324", {"start": v(-4.34, -13.14) * mm, "end": v(-4.32, -13.02) * mm});
            skLineSegment(sketch, "E325", {"start": v(-4.32, -13.02) * mm, "end": v(-4.3, -12.94) * mm});
            skLineSegment(sketch, "E326", {"start": v(-4.3, -12.94) * mm, "end": v(-4.29, -12.89) * mm});
            skLineSegment(sketch, "E327", {"start": v(-4.29, -12.89) * mm, "end": v(-4.28, -12.87) * mm});
            skLineSegment(sketch, "E328", {"start": v(-4.28, -12.87) * mm, "end": v(-4.13, -12.42) * mm});
            skArc(sketch, "E329", {"start": v(-4.13, -12.42) * mm, "mid": v(-4.62, -12.25) * mm, "end": v(-5.1, -12.06) * mm});
            skLineSegment(sketch, "E330", {"start": v(-5.1, -12.06) * mm, "end": v(-5.28, -12.5) * mm});
            skLineSegment(sketch, "E331", {"start": v(-5.28, -12.5) * mm, "end": v(-5.29, -12.51) * mm});
            skLineSegment(sketch, "E332", {"start": v(-5.29, -12.51) * mm, "end": v(-5.31, -12.56) * mm});
            skLineSegment(sketch, "E333", {"start": v(-5.31, -12.56) * mm, "end": v(-5.35, -12.63) * mm});
            skLineSegment(sketch, "E334", {"start": v(-5.35, -12.63) * mm, "end": v(-5.42, -12.73) * mm});
            skLineSegment(sketch, "E335", {"start": v(-5.42, -12.73) * mm, "end": v(-5.5, -12.85) * mm});
            skLineSegment(sketch, "E336", {"start": v(-5.5, -12.85) * mm, "end": v(-5.62, -13) * mm});
            skLineSegment(sketch, "E337", {"start": v(-5.62, -13) * mm, "end": v(-5.77, -13.16) * mm});
            skLineSegment(sketch, "E338", {"start": v(-5.77, -13.16) * mm, "end": v(-5.95, -13.35) * mm});
            skLineSegment(sketch, "E339", {"start": v(-5.95, -13.35) * mm, "end": v(-6.1, -13.5) * mm});
            skArc(sketch, "E340", {"start": v(-6.1, -13.5) * mm, "mid": v(-6.45, -13.34) * mm, "end": v(-6.78, -13.17) * mm});
            skLineSegment(sketch, "E341", {"start": v(-6.78, -13.17) * mm, "end": v(-6.76, -12.95) * mm});
            skLineSegment(sketch, "E342", {"start": v(-6.76, -12.95) * mm, "end": v(-6.73, -12.7) * mm});
            skLineSegment(sketch, "E343", {"start": v(-6.73, -12.7) * mm, "end": v(-6.7, -12.48) * mm});
            skLineSegment(sketch, "E344", {"start": v(-6.7, -12.48) * mm, "end": v(-6.65, -12.3) * mm});
            skLineSegment(sketch, "E345", {"start": v(-6.65, -12.3) * mm, "end": v(-6.6, -12.15) * mm});
            skLineSegment(sketch, "E346", {"start": v(-6.6, -12.15) * mm, "end": v(-6.57, -12.04) * mm});
            skLineSegment(sketch, "E347", {"start": v(-6.57, -12.04) * mm, "end": v(-6.54, -11.96) * mm});
            skLineSegment(sketch, "E348", {"start": v(-6.54, -11.96) * mm, "end": v(-6.52, -11.92) * mm});
            skLineSegment(sketch, "E349", {"start": v(-6.52, -11.92) * mm, "end": v(-6.51, -11.9) * mm});
            skLineSegment(sketch, "E350", {"start": v(-6.51, -11.9) * mm, "end": v(-6.28, -11.48) * mm});
            skArc(sketch, "E351", {"start": v(-6.28, -11.48) * mm, "mid": v(-6.73, -11.23) * mm, "end": v(-7.16, -10.95) * mm});
            skLineSegment(sketch, "E352", {"start": v(-7.16, -10.95) * mm, "end": v(-7.42, -11.35) * mm});
            skLineSegment(sketch, "E353", {"start": v(-7.42, -11.35) * mm, "end": v(-7.43, -11.37) * mm});
            skLineSegment(sketch, "E354", {"start": v(-7.43, -11.37) * mm, "end": v(-7.47, -11.4) * mm});
            skLineSegment(sketch, "E355", {"start": v(-7.47, -11.4) * mm, "end": v(-7.52, -11.47) * mm});
            skLineSegment(sketch, "E356", {"start": v(-7.52, -11.47) * mm, "end": v(-7.6, -11.56) * mm});
            skLineSegment(sketch, "E357", {"start": v(-7.6, -11.56) * mm, "end": v(-7.71, -11.66) * mm});
            skLineSegment(sketch, "E358", {"start": v(-7.71, -11.66) * mm, "end": v(-7.85, -11.79) * mm});
            skLineSegment(sketch, "E359", {"start": v(-7.85, -11.79) * mm, "end": v(-8.03, -11.92) * mm});
            skLineSegment(sketch, "E360", {"start": v(-8.03, -11.92) * mm, "end": v(-8.23, -12.07) * mm});
            skLineSegment(sketch, "E361", {"start": v(-8.23, -12.07) * mm, "end": v(-8.42, -12.19) * mm});
            skArc(sketch, "E362", {"start": v(-8.42, -12.19) * mm, "mid": v(-8.72, -11.97) * mm, "end": v(-9.02, -11.75) * mm});
            skLineSegment(sketch, "E363", {"start": v(-9.02, -11.75) * mm, "end": v(-8.96, -11.54) * mm});
            skLineSegment(sketch, "E364", {"start": v(-8.96, -11.54) * mm, "end": v(-8.89, -11.3) * mm});
            skLineSegment(sketch, "E365", {"start": v(-8.89, -11.3) * mm, "end": v(-8.81, -11.09) * mm});
            skLineSegment(sketch, "E366", {"start": v(-8.81, -11.09) * mm, "end": v(-8.74, -10.92) * mm});
            skLineSegment(sketch, "E367", {"start": v(-8.74, -10.92) * mm, "end": v(-8.67, -10.78) * mm});
            skLineSegment(sketch, "E368", {"start": v(-8.67, -10.78) * mm, "end": v(-8.61, -10.68) * mm});
            skLineSegment(sketch, "E369", {"start": v(-8.61, -10.68) * mm, "end": v(-8.57, -10.6) * mm});
            skLineSegment(sketch, "E370", {"start": v(-8.57, -10.6) * mm, "end": v(-8.54, -10.56) * mm});
            skLineSegment(sketch, "E371", {"start": v(-8.54, -10.56) * mm, "end": v(-8.53, -10.55) * mm});
            skLineSegment(sketch, "E372", {"start": v(-8.53, -10.55) * mm, "end": v(-8.23, -10.17) * mm});
            skArc(sketch, "E373", {"start": v(-8.23, -10.17) * mm, "mid": v(-8.62, -9.84) * mm, "end": v(-9, -9.5) * mm});
            skLineSegment(sketch, "E374", {"start": v(-9, -9.5) * mm, "end": v(-9.33, -9.85) * mm});
            skLineSegment(sketch, "E375", {"start": v(-9.33, -9.85) * mm, "end": v(-9.34, -9.86) * mm});
            skLineSegment(sketch, "E376", {"start": v(-9.34, -9.86) * mm, "end": v(-9.38, -9.9) * mm});
            skLineSegment(sketch, "E377", {"start": v(-9.38, -9.9) * mm, "end": v(-9.45, -9.95) * mm});
            skLineSegment(sketch, "E378", {"start": v(-9.45, -9.95) * mm, "end": v(-9.54, -10.02) * mm});
            skLineSegment(sketch, "E379", {"start": v(-9.54, -10.02) * mm, "end": v(-9.67, -10.1) * mm});
            skLineSegment(sketch, "E380", {"start": v(-9.67, -10.1) * mm, "end": v(-9.83, -10.2) * mm});
            skLineSegment(sketch, "E381", {"start": v(-9.83, -10.2) * mm, "end": v(-10.02, -10.3) * mm});
            skLineSegment(sketch, "E382", {"start": v(-10.02, -10.3) * mm, "end": v(-10.25, -10.4) * mm});
            skLineSegment(sketch, "E383", {"start": v(-10.25, -10.4) * mm, "end": v(-10.46, -10.49) * mm});
            skArc(sketch, "E384", {"start": v(-10.46, -10.49) * mm, "mid": v(-10.72, -10.22) * mm, "end": v(-10.97, -9.95) * mm});
            skLineSegment(sketch, "E385", {"start": v(-10.97, -9.95) * mm, "end": v(-10.88, -9.75) * mm});
            skLineSegment(sketch, "E386", {"start": v(-10.88, -9.75) * mm, "end": v(-10.76, -9.53) * mm});
            skLineSegment(sketch, "E387", {"start": v(-10.76, -9.53) * mm, "end": v(-10.65, -9.34) * mm});
            skLineSegment(sketch, "E388", {"start": v(-10.65, -9.34) * mm, "end": v(-10.54, -9.18) * mm});
            skLineSegment(sketch, "E389", {"start": v(-10.54, -9.18) * mm, "end": v(-10.45, -9.06) * mm});
            skLineSegment(sketch, "E390", {"start": v(-10.45, -9.06) * mm, "end": v(-10.38, -8.97) * mm});
            skLineSegment(sketch, "E391", {"start": v(-10.38, -8.97) * mm, "end": v(-10.32, -8.9) * mm});
            skLineSegment(sketch, "E392", {"start": v(-10.32, -8.9) * mm, "end": v(-10.29, -8.87) * mm});
            skLineSegment(sketch, "E393", {"start": v(-10.29, -8.87) * mm, "end": v(-10.27, -8.86) * mm});
            skLineSegment(sketch, "E394", {"start": v(-10.27, -8.86) * mm, "end": v(-9.9, -8.54) * mm});
            skArc(sketch, "E395", {"start": v(-9.9, -8.54) * mm, "mid": v(-10.24, -8.15) * mm, "end": v(-10.55, -7.74) * mm});
            skLineSegment(sketch, "E396", {"start": v(-10.55, -7.74) * mm, "end": v(-10.94, -8.02) * mm});
            skLineSegment(sketch, "E397", {"start": v(-10.94, -8.02) * mm, "end": v(-10.95, -8.03) * mm});
            skLineSegment(sketch, "E398", {"start": v(-10.95, -8.03) * mm, "end": v(-11, -8.06) * mm});
            skLineSegment(sketch, "E399", {"start": v(-11, -8.06) * mm, "end": v(-11.07, -8.1) * mm});
            skLineSegment(sketch, "E400", {"start": v(-11.07, -8.1) * mm, "end": v(-11.17, -8.15) * mm});
            skLineSegment(sketch, "E401", {"start": v(-11.17, -8.15) * mm, "end": v(-11.31, -8.21) * mm});
            skLineSegment(sketch, "E402", {"start": v(-11.31, -8.21) * mm, "end": v(-11.49, -8.28) * mm});
            skLineSegment(sketch, "E403", {"start": v(-11.49, -8.28) * mm, "end": v(-11.7, -8.34) * mm});
            skLineSegment(sketch, "E404", {"start": v(-11.7, -8.34) * mm, "end": v(-11.94, -8.4) * mm});
            skLineSegment(sketch, "E405", {"start": v(-11.94, -8.4) * mm, "end": v(-12.16, -8.45) * mm});
            skArc(sketch, "E406", {"start": v(-12.16, -8.45) * mm, "mid": v(-12.37, -8.14) * mm, "end": v(-12.57, -7.83) * mm});
            skLineSegment(sketch, "E407", {"start": v(-12.57, -7.83) * mm, "end": v(-12.44, -7.65) * mm});
            skLineSegment(sketch, "E408", {"start": v(-12.44, -7.65) * mm, "end": v(-12.28, -7.45) * mm});
            skLineSegment(sketch, "E409", {"start": v(-12.28, -7.45) * mm, "end": v(-12.14, -7.28) * mm});
            skLineSegment(sketch, "E410", {"start": v(-12.14, -7.28) * mm, "end": v(-12.01, -7.15) * mm});
            skLineSegment(sketch, "E411", {"start": v(-12.01, -7.15) * mm, "end": v(-11.9, -7.05) * mm});
            skLineSegment(sketch, "E412", {"start": v(-11.9, -7.05) * mm, "end": v(-11.8, -6.97) * mm});
            skLineSegment(sketch, "E413", {"start": v(-11.8, -6.97) * mm, "end": v(-11.74, -6.92) * mm});
            skLineSegment(sketch, "E414", {"start": v(-11.74, -6.92) * mm, "end": v(-11.7, -6.89) * mm});
            skLineSegment(sketch, "E415", {"start": v(-11.7, -6.89) * mm, "end": v(-11.69, -6.88) * mm});
            skLineSegment(sketch, "E416", {"start": v(-11.69, -6.88) * mm, "end": v(-11.27, -6.64) * mm});
            skArc(sketch, "E417", {"start": v(-11.27, -6.64) * mm, "mid": v(-11.52, -6.19) * mm, "end": v(-11.76, -5.73) * mm});
            skLineSegment(sketch, "E418", {"start": v(-11.76, -5.73) * mm, "end": v(-12.19, -5.94) * mm});
            skLineSegment(sketch, "E419", {"start": v(-12.19, -5.94) * mm, "end": v(-12.2, -5.95) * mm});
            skLineSegment(sketch, "E420", {"start": v(-12.2, -5.95) * mm, "end": v(-12.25, -5.97) * mm});
            skLineSegment(sketch, "E421", {"start": v(-12.25, -5.97) * mm, "end": v(-12.33, -6) * mm});
            skLineSegment(sketch, "E422", {"start": v(-12.33, -6) * mm, "end": v(-12.45, -6.03) * mm});
            skLineSegment(sketch, "E423", {"start": v(-12.45, -6.03) * mm, "end": v(-12.6, -6.06) * mm});
            skLineSegment(sketch, "E424", {"start": v(-12.6, -6.06) * mm, "end": v(-12.78, -6.1) * mm});
            skLineSegment(sketch, "E425", {"start": v(-12.78, -6.1) * mm, "end": v(-13, -6.12) * mm});
            skLineSegment(sketch, "E426", {"start": v(-13, -6.12) * mm, "end": v(-13.25, -6.14) * mm});
            skLineSegment(sketch, "E427", {"start": v(-13.25, -6.14) * mm, "end": v(-13.47, -6.15) * mm});
            skArc(sketch, "E428", {"start": v(-13.47, -6.15) * mm, "mid": v(-13.62, -5.8) * mm, "end": v(-13.76, -5.46) * mm});
            skLineSegment(sketch, "E429", {"start": v(-13.76, -5.46) * mm, "end": v(-13.6, -5.3) * mm});
            skLineSegment(sketch, "E430", {"start": v(-13.6, -5.3) * mm, "end": v(-13.41, -5.14) * mm});
            skLineSegment(sketch, "E431", {"start": v(-13.41, -5.14) * mm, "end": v(-13.24, -5) * mm});
            skLineSegment(sketch, "E432", {"start": v(-13.24, -5) * mm, "end": v(-13.1, -4.9) * mm});
            skLineSegment(sketch, "E433", {"start": v(-13.1, -4.9) * mm, "end": v(-12.96, -4.8) * mm});
            skLineSegment(sketch, "E434", {"start": v(-12.96, -4.8) * mm, "end": v(-12.86, -4.75) * mm});
            skLineSegment(sketch, "E435", {"start": v(-12.86, -4.75) * mm, "end": v(-12.79, -4.7) * mm});
            skLineSegment(sketch, "E436", {"start": v(-12.79, -4.7) * mm, "end": v(-12.74, -4.69) * mm});
            skLineSegment(sketch, "E437", {"start": v(-12.74, -4.69) * mm, "end": v(-12.72, -4.68) * mm});
            skLineSegment(sketch, "E438", {"start": v(-12.72, -4.68) * mm, "end": v(-12.27, -4.52) * mm});
            skArc(sketch, "E439", {"start": v(-12.27, -4.52) * mm, "mid": v(-12.44, -4.03) * mm, "end": v(-12.59, -3.54) * mm});
            skLineSegment(sketch, "E440", {"start": v(-12.59, -3.54) * mm, "end": v(-13.05, -3.67) * mm});
            skLineSegment(sketch, "E441", {"start": v(-13.05, -3.67) * mm, "end": v(-13.07, -3.67) * mm});
            skLineSegment(sketch, "E442", {"start": v(-13.07, -3.67) * mm, "end": v(-13.12, -3.68) * mm});
            skLineSegment(sketch, "E443", {"start": v(-13.12, -3.68) * mm, "end": v(-13.2, -3.7) * mm});
            skLineSegment(sketch, "E444", {"start": v(-13.2, -3.7) * mm, "end": v(-13.32, -3.7) * mm});
            skLineSegment(sketch, "E445", {"start": v(-13.32, -3.7) * mm, "end": v(-13.47, -3.71) * mm});
            skLineSegment(sketch, "E446", {"start": v(-13.47, -3.71) * mm, "end": v(-13.66, -3.71) * mm});
            skLineSegment(sketch, "E447", {"start": v(-13.66, -3.71) * mm, "end": v(-13.88, -3.7) * mm});
            skLineSegment(sketch, "E448", {"start": v(-13.88, -3.7) * mm, "end": v(-14.13, -3.67) * mm});
            skLineSegment(sketch, "E449", {"start": v(-14.13, -3.67) * mm, "end": v(-14.35, -3.64) * mm});
            skArc(sketch, "E450", {"start": v(-14.35, -3.64) * mm, "mid": v(-14.43, -3.28) * mm, "end": v(-14.51, -2.92) * mm});
            skLineSegment(sketch, "E451", {"start": v(-14.51, -2.92) * mm, "end": v(-14.33, -2.8) * mm});
            skLineSegment(sketch, "E452", {"start": v(-14.33, -2.8) * mm, "end": v(-14.11, -2.66) * mm});
            skLineSegment(sketch, "E453", {"start": v(-14.11, -2.66) * mm, "end": v(-13.92, -2.56) * mm});
            skLineSegment(sketch, "E454", {"start": v(-13.92, -2.56) * mm, "end": v(-13.75, -2.47) * mm});
            skLineSegment(sketch, "E455", {"start": v(-13.75, -2.47) * mm, "end": v(-13.61, -2.42) * mm});
            skLineSegment(sketch, "E456", {"start": v(-13.61, -2.42) * mm, "end": v(-13.5, -2.38) * mm});
            skLineSegment(sketch, "E457", {"start": v(-13.5, -2.38) * mm, "end": v(-13.42, -2.35) * mm});
            skLineSegment(sketch, "E458", {"start": v(-13.42, -2.35) * mm, "end": v(-13.37, -2.34) * mm});
            skLineSegment(sketch, "E459", {"start": v(-13.37, -2.34) * mm, "end": v(-13.35, -2.33) * mm});
            skLineSegment(sketch, "E460", {"start": v(-13.35, -2.33) * mm, "end": v(-12.88, -2.25) * mm});
            skArc(sketch, "E461", {"start": v(-12.88, -2.25) * mm, "mid": v(-12.96, -1.74) * mm, "end": v(-13.02, -1.23) * mm});
            skLineSegment(sketch, "E462", {"start": v(-13.02, -1.23) * mm, "end": v(-13.5, -1.28) * mm});
            skLineSegment(sketch, "E463", {"start": v(-13.5, -1.28) * mm, "end": v(-13.51, -1.28) * mm});
            skLineSegment(sketch, "E464", {"start": v(-13.51, -1.28) * mm, "end": v(-13.56, -1.28) * mm});
            skLineSegment(sketch, "E465", {"start": v(-13.56, -1.28) * mm, "end": v(-13.65, -1.28) * mm});
            skLineSegment(sketch, "E466", {"start": v(-13.65, -1.28) * mm, "end": v(-13.76, -1.27) * mm});
            skLineSegment(sketch, "E467", {"start": v(-13.76, -1.27) * mm, "end": v(-13.92, -1.25) * mm});
            skLineSegment(sketch, "E468", {"start": v(-13.92, -1.25) * mm, "end": v(-14.1, -1.21) * mm});
            skLineSegment(sketch, "E469", {"start": v(-14.1, -1.21) * mm, "end": v(-14.31, -1.16) * mm});
            skLineSegment(sketch, "E470", {"start": v(-14.31, -1.16) * mm, "end": v(-14.56, -1.1) * mm});
            skLineSegment(sketch, "E471", {"start": v(-14.56, -1.1) * mm, "end": v(-14.77, -1.02) * mm});
            skArc(sketch, "E472", {"start": v(-14.77, -1.02) * mm, "mid": v(-14.79, -0.65) * mm, "end": v(-14.8, -0.28) * mm});
            skLineSegment(sketch, "E473", {"start": v(-14.8, -0.28) * mm, "end": v(-14.6, -0.19) * mm});
            skLineSegment(sketch, "E474", {"start": v(-14.6, -0.19) * mm, "end": v(-14.36, -0.1) * mm});
            skLineSegment(sketch, "E475", {"start": v(-14.36, -0.1) * mm, "end": v(-14.15, -0.03) * mm});
            skLineSegment(sketch, "E476", {"start": v(-14.15, -0.03) * mm, "end": v(-13.97, 0.02) * mm});
            skLineSegment(sketch, "E477", {"start": v(-13.97, 0.02) * mm, "end": v(-13.82, 0.05) * mm});
            skLineSegment(sketch, "E478", {"start": v(-13.82, 0.05) * mm, "end": v(-13.7, 0.07) * mm});
            skLineSegment(sketch, "E479", {"start": v(-13.7, 0.07) * mm, "end": v(-13.62, 0.08) * mm});
            skLineSegment(sketch, "E480", {"start": v(-13.62, 0.08) * mm, "end": v(-13.57, 0.09) * mm});
            skLineSegment(sketch, "E481", {"start": v(-13.57, 0.09) * mm, "end": v(-13.55, 0.09) * mm});
            skLineSegment(sketch, "E482", {"start": v(-13.55, 0.09) * mm, "end": v(-13.07, 0.08) * mm});
            skArc(sketch, "E483", {"start": v(-13.07, 0.08) * mm, "mid": v(-13.06, 0.6) * mm, "end": v(-13.03, 1.1) * mm});
            skLineSegment(sketch, "E484", {"start": v(-13.03, 1.1) * mm, "end": v(-13.5, 1.15) * mm});
            skLineSegment(sketch, "E485", {"start": v(-13.5, 1.15) * mm, "end": v(-13.52, 1.15) * mm});
            skLineSegment(sketch, "E486", {"start": v(-13.52, 1.15) * mm, "end": v(-13.57, 1.16) * mm});
            skLineSegment(sketch, "E487", {"start": v(-13.57, 1.16) * mm, "end": v(-13.65, 1.18) * mm});
            skLineSegment(sketch, "E488", {"start": v(-13.65, 1.18) * mm, "end": v(-13.77, 1.2) * mm});
            skLineSegment(sketch, "E489", {"start": v(-13.77, 1.2) * mm, "end": v(-13.91, 1.26) * mm});
            skLineSegment(sketch, "E490", {"start": v(-13.91, 1.26) * mm, "end": v(-14.09, 1.32) * mm});
            skLineSegment(sketch, "E491", {"start": v(-14.09, 1.32) * mm, "end": v(-14.29, 1.41) * mm});
            skLineSegment(sketch, "E492", {"start": v(-14.29, 1.41) * mm, "end": v(-14.52, 1.52) * mm});
            skLineSegment(sketch, "E493", {"start": v(-14.52, 1.52) * mm, "end": v(-14.7, 1.63) * mm});
            skArc(sketch, "E494", {"start": v(-14.7, 1.63) * mm, "mid": v(-14.66, 2) * mm, "end": v(-14.6, 2.37) * mm});
            skLineSegment(sketch, "E495", {"start": v(-14.6, 2.37) * mm, "end": v(-14.4, 2.42) * mm});
            skLineSegment(sketch, "E496", {"start": v(-14.4, 2.42) * mm, "end": v(-14.14, 2.47) * mm});
            skLineSegment(sketch, "E497", {"start": v(-14.14, 2.47) * mm, "end": v(-13.93, 2.5) * mm});
            skLineSegment(sketch, "E498", {"start": v(-13.93, 2.5) * mm, "end": v(-13.74, 2.51) * mm});
            skLineSegment(sketch, "E499", {"start": v(-13.74, 2.51) * mm, "end": v(-13.59, 2.52) * mm});
            skLineSegment(sketch, "E500", {"start": v(-13.59, 2.52) * mm, "end": v(-13.47, 2.52) * mm});
            skLineSegment(sketch, "E501", {"start": v(-13.47, 2.52) * mm, "end": v(-13.38, 2.51) * mm});
            skLineSegment(sketch, "E502", {"start": v(-13.38, 2.51) * mm, "end": v(-13.33, 2.5) * mm});
            skLineSegment(sketch, "E503", {"start": v(-13.33, 2.5) * mm, "end": v(-13.32, 2.5) * mm});
            skLineSegment(sketch, "E504", {"start": v(-13.32, 2.5) * mm, "end": v(-12.85, 2.42) * mm});
            skArc(sketch, "E505", {"start": v(-12.85, 2.42) * mm, "mid": v(-12.74, 2.92) * mm, "end": v(-12.62, 3.42) * mm});
            skLineSegment(sketch, "E506", {"start": v(-12.62, 3.42) * mm, "end": v(-13.08, 3.54) * mm});
            skLineSegment(sketch, "E507", {"start": v(-13.08, 3.54) * mm, "end": v(-13.1, 3.55) * mm});
            skLineSegment(sketch, "E508", {"start": v(-13.1, 3.55) * mm, "end": v(-13.14, 3.57) * mm});
            skLineSegment(sketch, "E509", {"start": v(-13.14, 3.57) * mm, "end": v(-13.22, 3.6) * mm});
            skLineSegment(sketch, "E510", {"start": v(-13.22, 3.6) * mm, "end": v(-13.33, 3.65) * mm});
            skLineSegment(sketch, "E511", {"start": v(-13.33, 3.65) * mm, "end": v(-13.46, 3.72) * mm});
            skLineSegment(sketch, "E512", {"start": v(-13.46, 3.72) * mm, "end": v(-13.62, 3.82) * mm});
            skLineSegment(sketch, "E513", {"start": v(-13.62, 3.82) * mm, "end": v(-13.8, 3.94) * mm});
            skLineSegment(sketch, "E514", {"start": v(-13.8, 3.94) * mm, "end": v(-14, 4.1) * mm});
            skLineSegment(sketch, "E515", {"start": v(-14, 4.1) * mm, "end": v(-14.18, 4.23) * mm});
            skArc(sketch, "E516", {"start": v(-14.18, 4.23) * mm, "mid": v(-14.07, 4.59) * mm, "end": v(-13.95, 4.94) * mm});
            skLineSegment(sketch, "E517", {"start": v(-13.95, 4.94) * mm, "end": v(-13.73, 4.95) * mm});
            skLineSegment(sketch, "E518", {"start": v(-13.73, 4.95) * mm, "end": v(-13.47, 4.95) * mm});
            skLineSegment(sketch, "E519", {"start": v(-13.47, 4.95) * mm, "end": v(-13.25, 4.94) * mm});
            skLineSegment(sketch, "E520", {"start": v(-13.25, 4.94) * mm, "end": v(-13.07, 4.93) * mm});
            skLineSegment(sketch, "E521", {"start": v(-13.07, 4.93) * mm, "end": v(-12.92, 4.9) * mm});
            skLineSegment(sketch, "E522", {"start": v(-12.92, 4.9) * mm, "end": v(-12.8, 4.88) * mm});
            skLineSegment(sketch, "E523", {"start": v(-12.8, 4.88) * mm, "end": v(-12.72, 4.86) * mm});
            skLineSegment(sketch, "E524", {"start": v(-12.72, 4.86) * mm, "end": v(-12.67, 4.85) * mm});
            skLineSegment(sketch, "E525", {"start": v(-12.67, 4.85) * mm, "end": v(-12.65, 4.84) * mm});
            skLineSegment(sketch, "E526", {"start": v(-12.65, 4.84) * mm, "end": v(-12.2, 4.67) * mm});
            skArc(sketch, "E527", {"start": v(-12.2, 4.67) * mm, "mid": v(-12.01, 5.15) * mm, "end": v(-11.8, 5.62) * mm});
            skLineSegment(sketch, "E528", {"start": v(-11.8, 5.62) * mm, "end": v(-12.23, 5.82) * mm});
            skLineSegment(sketch, "E529", {"start": v(-12.23, 5.82) * mm, "end": v(-12.25, 5.83) * mm});
            skLineSegment(sketch, "E530", {"start": v(-12.25, 5.83) * mm, "end": v(-12.3, 5.85) * mm});
            skLineSegment(sketch, "E531", {"start": v(-12.3, 5.85) * mm, "end": v(-12.36, 5.9) * mm});
            skLineSegment(sketch, "E532", {"start": v(-12.36, 5.9) * mm, "end": v(-12.46, 5.97) * mm});
            skLineSegment(sketch, "E533", {"start": v(-12.46, 5.97) * mm, "end": v(-12.58, 6.06) * mm});
            skLineSegment(sketch, "E534", {"start": v(-12.58, 6.06) * mm, "end": v(-12.72, 6.19) * mm});
            skLineSegment(sketch, "E535", {"start": v(-12.72, 6.19) * mm, "end": v(-12.88, 6.34) * mm});
            skLineSegment(sketch, "E536", {"start": v(-12.88, 6.34) * mm, "end": v(-13.05, 6.53) * mm});
            skLineSegment(sketch, "E537", {"start": v(-13.05, 6.53) * mm, "end": v(-13.2, 6.7) * mm});
            skArc(sketch, "E538", {"start": v(-13.2, 6.7) * mm, "mid": v(-13.02, 7.02) * mm, "end": v(-12.84, 7.35) * mm});
            skLineSegment(sketch, "E539", {"start": v(-12.84, 7.35) * mm, "end": v(-12.62, 7.32) * mm});
            skLineSegment(sketch, "E540", {"start": v(-12.62, 7.32) * mm, "end": v(-12.37, 7.28) * mm});
            skLineSegment(sketch, "E541", {"start": v(-12.37, 7.28) * mm, "end": v(-12.15, 7.23) * mm});
            skLineSegment(sketch, "E542", {"start": v(-12.15, 7.23) * mm, "end": v(-11.98, 7.18) * mm});
            skLineSegment(sketch, "E543", {"start": v(-11.98, 7.18) * mm, "end": v(-11.83, 7.13) * mm});
            skLineSegment(sketch, "E544", {"start": v(-11.83, 7.13) * mm, "end": v(-11.72, 7.1) * mm});
            skLineSegment(sketch, "E545", {"start": v(-11.72, 7.1) * mm, "end": v(-11.64, 7.06) * mm});
            skLineSegment(sketch, "E546", {"start": v(-11.64, 7.06) * mm, "end": v(-11.6, 7.03) * mm});
            skLineSegment(sketch, "E547", {"start": v(-11.6, 7.03) * mm, "end": v(-11.58, 7.02) * mm});
            skLineSegment(sketch, "E548", {"start": v(-11.58, 7.02) * mm, "end": v(-11.17, 6.78) * mm});
            skArc(sketch, "E549", {"start": v(-11.17, 6.78) * mm, "mid": v(-10.9, 7.2) * mm, "end": v(-10.6, 7.63) * mm});
            skLineSegment(sketch, "E550", {"start": v(-10.6, 7.63) * mm, "end": v(-11, 7.91) * mm});
            skLineSegment(sketch, "E551", {"start": v(-11, 7.91) * mm, "end": v(-11, 7.92) * mm});
            skLineSegment(sketch, "E552", {"start": v(-11, 7.92) * mm, "end": v(-11.05, 7.96) * mm});
            skLineSegment(sketch, "E553", {"start": v(-11.05, 7.96) * mm, "end": v(-11.1, 8.01) * mm});
            skLineSegment(sketch, "E554", {"start": v(-11.1, 8.01) * mm, "end": v(-11.2, 8.1) * mm});
            skLineSegment(sketch, "E555", {"start": v(-11.2, 8.1) * mm, "end": v(-11.3, 8.21) * mm});
            skLineSegment(sketch, "E556", {"start": v(-11.3, 8.21) * mm, "end": v(-11.4, 8.36) * mm});
            skLineSegment(sketch, "E557", {"start": v(-11.4, 8.36) * mm, "end": v(-11.54, 8.54) * mm});
            skLineSegment(sketch, "E558", {"start": v(-11.54, 8.54) * mm, "end": v(-11.67, 8.75) * mm});
            skLineSegment(sketch, "E559", {"start": v(-11.67, 8.75) * mm, "end": v(-11.78, 8.94) * mm});
            skArc(sketch, "E560", {"start": v(-11.78, 8.94) * mm, "mid": v(-11.55, 9.24) * mm, "end": v(-11.32, 9.52) * mm});
            skLineSegment(sketch, "E561", {"start": v(-11.32, 9.52) * mm, "end": v(-11.1, 9.46) * mm});
            skLineSegment(sketch, "E562", {"start": v(-11.1, 9.46) * mm, "end": v(-10.87, 9.37) * mm});
            skLineSegment(sketch, "E563", {"start": v(-10.87, 9.37) * mm, "end": v(-10.67, 9.28) * mm});
            skLineSegment(sketch, "E564", {"start": v(-10.67, 9.28) * mm, "end": v(-10.5, 9.2) * mm});
            skLineSegment(sketch, "E565", {"start": v(-10.5, 9.2) * mm, "end": v(-10.36, 9.13) * mm});
            skLineSegment(sketch, "E566", {"start": v(-10.36, 9.13) * mm, "end": v(-10.26, 9.07) * mm});
            skLineSegment(sketch, "E567", {"start": v(-10.26, 9.07) * mm, "end": v(-10.2, 9.02) * mm});
            skLineSegment(sketch, "E568", {"start": v(-10.2, 9.02) * mm, "end": v(-10.15, 9) * mm});
            skLineSegment(sketch, "E569", {"start": v(-10.15, 9) * mm, "end": v(-10.14, 8.98) * mm});
            skLineSegment(sketch, "E570", {"start": v(-10.14, 8.98) * mm, "end": v(-9.78, 8.66) * mm});
            skArc(sketch, "E571", {"start": v(-9.78, 8.66) * mm, "mid": v(-9.43, 9.04) * mm, "end": v(-9.07, 9.4) * mm});
            skLineSegment(sketch, "E572", {"start": v(-9.07, 9.4) * mm, "end": v(-9.4, 9.75) * mm});
            skLineSegment(sketch, "E573", {"start": v(-9.4, 9.75) * mm, "end": v(-9.41, 9.76) * mm});
            skLineSegment(sketch, "E574", {"start": v(-9.41, 9.76) * mm, "end": v(-9.45, 9.8) * mm});
            skLineSegment(sketch, "E575", {"start": v(-9.45, 9.8) * mm, "end": v(-9.5, 9.87) * mm});
            skLineSegment(sketch, "E576", {"start": v(-9.5, 9.87) * mm, "end": v(-9.56, 9.97) * mm});
            skLineSegment(sketch, "E577", {"start": v(-9.56, 9.97) * mm, "end": v(-9.64, 10.1) * mm});
            skLineSegment(sketch, "E578", {"start": v(-9.64, 10.1) * mm, "end": v(-9.73, 10.26) * mm});
            skLineSegment(sketch, "E579", {"start": v(-9.73, 10.26) * mm, "end": v(-9.82, 10.46) * mm});
            skLineSegment(sketch, "E580", {"start": v(-9.82, 10.46) * mm, "end": v(-9.92, 10.7) * mm});
            skLineSegment(sketch, "E581", {"start": v(-9.92, 10.7) * mm, "end": v(-10, 10.9) * mm});
            skArc(sketch, "E582", {"start": v(-10, 10.9) * mm, "mid": v(-9.72, 11.15) * mm, "end": v(-9.43, 11.4) * mm});
            skLineSegment(sketch, "E583", {"start": v(-9.43, 11.4) * mm, "end": v(-9.24, 11.29) * mm});
            skLineSegment(sketch, "E584", {"start": v(-9.24, 11.29) * mm, "end": v(-9.02, 11.16) * mm});
            skLineSegment(sketch, "E585", {"start": v(-9.02, 11.16) * mm, "end": v(-8.83, 11.04) * mm});
            skLineSegment(sketch, "E586", {"start": v(-8.83, 11.04) * mm, "end": v(-8.68, 10.93) * mm});
            skLineSegment(sketch, "E587", {"start": v(-8.68, 10.93) * mm, "end": v(-8.56, 10.83) * mm});
            skLineSegment(sketch, "E588", {"start": v(-8.56, 10.83) * mm, "end": v(-8.48, 10.76) * mm});
            skLineSegment(sketch, "E589", {"start": v(-8.48, 10.76) * mm, "end": v(-8.42, 10.7) * mm});
            skLineSegment(sketch, "E590", {"start": v(-8.42, 10.7) * mm, "end": v(-8.38, 10.66) * mm});
            skLineSegment(sketch, "E591", {"start": v(-8.38, 10.66) * mm, "end": v(-8.37, 10.65) * mm});
            skLineSegment(sketch, "E592", {"start": v(-8.37, 10.65) * mm, "end": v(-8.07, 10.27) * mm});
            skArc(sketch, "E593", {"start": v(-8.07, 10.27) * mm, "mid": v(-7.66, 10.58) * mm, "end": v(-7.24, 10.87) * mm});
            skLineSegment(sketch, "E594", {"start": v(-7.24, 10.87) * mm, "end": v(-7.5, 11.27) * mm});
            skLineSegment(sketch, "E595", {"start": v(-7.5, 11.27) * mm, "end": v(-7.52, 11.28) * mm});
            skLineSegment(sketch, "E596", {"start": v(-7.52, 11.28) * mm, "end": v(-7.54, 11.33) * mm});
            skLineSegment(sketch, "E597", {"start": v(-7.54, 11.33) * mm, "end": v(-7.58, 11.4) * mm});
            skLineSegment(sketch, "E598", {"start": v(-7.58, 11.4) * mm, "end": v(-7.63, 11.51) * mm});
            skLineSegment(sketch, "E599", {"start": v(-7.63, 11.51) * mm, "end": v(-7.68, 11.66) * mm});
            skLineSegment(sketch, "E600", {"start": v(-7.68, 11.66) * mm, "end": v(-7.74, 11.83) * mm});
            skLineSegment(sketch, "E601", {"start": v(-7.74, 11.83) * mm, "end": v(-7.8, 12.05) * mm});
            skLineSegment(sketch, "E602", {"start": v(-7.8, 12.05) * mm, "end": v(-7.85, 12.3) * mm});
            skLineSegment(sketch, "E603", {"start": v(-7.85, 12.3) * mm, "end": v(-7.88, 12.51) * mm});
            skArc(sketch, "E604", {"start": v(-7.88, 12.51) * mm, "mid": v(-7.57, 12.7) * mm, "end": v(-7.24, 12.9) * mm});
            skLineSegment(sketch, "E605", {"start": v(-7.24, 12.9) * mm, "end": v(-7.07, 12.76) * mm});
            skLineSegment(sketch, "E606", {"start": v(-7.07, 12.76) * mm, "end": v(-6.88, 12.6) * mm});
            skLineSegment(sketch, "E607", {"start": v(-6.88, 12.6) * mm, "end": v(-6.72, 12.44) * mm});
            skLineSegment(sketch, "E608", {"start": v(-6.72, 12.44) * mm, "end": v(-6.59, 12.3) * mm});
            skLineSegment(sketch, "E609", {"start": v(-6.59, 12.3) * mm, "end": v(-6.49, 12.19) * mm});
            skLineSegment(sketch, "E610", {"start": v(-6.49, 12.19) * mm, "end": v(-6.42, 12.1) * mm});
            skLineSegment(sketch, "E611", {"start": v(-6.42, 12.1) * mm, "end": v(-6.37, 12.03) * mm});
            skLineSegment(sketch, "E612", {"start": v(-6.37, 12.03) * mm, "end": v(-6.34, 11.98) * mm});
            skLineSegment(sketch, "E613", {"start": v(-6.34, 11.98) * mm, "end": v(-6.33, 11.97) * mm});
            skLineSegment(sketch, "E614", {"start": v(-6.33, 11.97) * mm, "end": v(-6.1, 11.54) * mm});
            skArc(sketch, "E615", {"start": v(-6.1, 11.54) * mm, "mid": v(-5.65, 11.78) * mm, "end": v(-5.18, 11.99) * mm});
            skLineSegment(sketch, "E616", {"start": v(-5.18, 11.99) * mm, "end": v(-5.37, 12.43) * mm});
            skLineSegment(sketch, "E617", {"start": v(-5.37, 12.43) * mm, "end": v(-5.38, 12.44) * mm});
            skLineSegment(sketch, "E618", {"start": v(-5.38, 12.44) * mm, "end": v(-5.4, 12.5) * mm});
            skLineSegment(sketch, "E619", {"start": v(-5.4, 12.5) * mm, "end": v(-5.42, 12.57) * mm});
            skLineSegment(sketch, "E620", {"start": v(-5.42, 12.57) * mm, "end": v(-5.45, 12.69) * mm});
            skLineSegment(sketch, "E621", {"start": v(-5.45, 12.69) * mm, "end": v(-5.47, 12.84) * mm});
            skLineSegment(sketch, "E622", {"start": v(-5.47, 12.84) * mm, "end": v(-5.5, 13.02) * mm});
            skLineSegment(sketch, "E623", {"start": v(-5.5, 13.02) * mm, "end": v(-5.52, 13.24) * mm});
            skLineSegment(sketch, "E624", {"start": v(-5.52, 13.24) * mm, "end": v(-5.52, 13.5) * mm});
            skLineSegment(sketch, "E625", {"start": v(-5.52, 13.5) * mm, "end": v(-5.52, 13.72) * mm});
            skArc(sketch, "E626", {"start": v(-5.52, 13.72) * mm, "mid": v(-5.17, 13.85) * mm, "end": v(-4.82, 13.98) * mm});
            skLineSegment(sketch, "E627", {"start": v(-4.82, 13.98) * mm, "end": v(-4.68, 13.81) * mm});
            skLineSegment(sketch, "E628", {"start": v(-4.68, 13.81) * mm, "end": v(-4.52, 13.62) * mm});
            skLineSegment(sketch, "E629", {"start": v(-4.52, 13.62) * mm, "end": v(-4.39, 13.44) * mm});
            skLineSegment(sketch, "E630", {"start": v(-4.39, 13.44) * mm, "end": v(-4.28, 13.28) * mm});
            skLineSegment(sketch, "E631", {"start": v(-4.28, 13.28) * mm, "end": v(-4.2, 13.15) * mm});
            skLineSegment(sketch, "E632", {"start": v(-4.2, 13.15) * mm, "end": v(-4.15, 13.05) * mm});
            skLineSegment(sketch, "E633", {"start": v(-4.15, 13.05) * mm, "end": v(-4.12, 12.97) * mm});
            skLineSegment(sketch, "E634", {"start": v(-4.12, 12.97) * mm, "end": v(-4.1, 12.92) * mm});
            skLineSegment(sketch, "E635", {"start": v(-4.1, 12.92) * mm, "end": v(-4.1, 12.9) * mm});
            skLineSegment(sketch, "E636", {"start": v(-4.1, 12.9) * mm, "end": v(-3.95, 12.45) * mm});
            skArc(sketch, "E637", {"start": v(-3.95, 12.45) * mm, "mid": v(-3.45, 12.6) * mm, "end": v(-2.96, 12.72) * mm});
            skLineSegment(sketch, "E638", {"start": v(-2.96, 12.72) * mm, "end": v(-3.06, 13.19) * mm});
            skLineSegment(sketch, "E639", {"start": v(-3.06, 13.19) * mm, "end": v(-3.07, 13.2) * mm});
            skLineSegment(sketch, "E640", {"start": v(-3.07, 13.2) * mm, "end": v(-3.07, 13.26) * mm});
            skLineSegment(sketch, "E641", {"start": v(-3.07, 13.26) * mm, "end": v(-3.08, 13.34) * mm});
            skLineSegment(sketch, "E642", {"start": v(-3.08, 13.34) * mm, "end": v(-3.09, 13.46) * mm});
            skLineSegment(sketch, "E643", {"start": v(-3.09, 13.46) * mm, "end": v(-3.09, 13.61) * mm});
            skLineSegment(sketch, "E644", {"start": v(-3.09, 13.61) * mm, "end": v(-3.08, 13.8) * mm});
            skLineSegment(sketch, "E645", {"start": v(-3.08, 13.8) * mm, "end": v(-3.06, 14.02) * mm});
            skLineSegment(sketch, "E646", {"start": v(-3.06, 14.02) * mm, "end": v(-3.02, 14.27) * mm});
            skLineSegment(sketch, "E647", {"start": v(-3.02, 14.27) * mm, "end": v(-2.98, 14.48) * mm});
            skArc(sketch, "E648", {"start": v(-2.98, 14.48) * mm, "mid": v(-2.61, 14.55) * mm, "end": v(-2.25, 14.61) * mm});
            skLineSegment(sketch, "E649", {"start": v(-2.25, 14.61) * mm, "end": v(-2.13, 14.43) * mm});
            skLineSegment(sketch, "E650", {"start": v(-2.13, 14.43) * mm, "end": v(-2, 14.2) * mm});
            skLineSegment(sketch, "E651", {"start": v(-2, 14.2) * mm, "end": v(-1.91, 14) * mm});
            skLineSegment(sketch, "E652", {"start": v(-1.91, 14) * mm, "end": v(-1.84, 13.83) * mm});
            skLineSegment(sketch, "E653", {"start": v(-1.84, 13.83) * mm, "end": v(-1.79, 13.7) * mm});
            skLineSegment(sketch, "E654", {"start": v(-1.79, 13.7) * mm, "end": v(-1.75, 13.58) * mm});
            skLineSegment(sketch, "E655", {"start": v(-1.75, 13.58) * mm, "end": v(-1.73, 13.5) * mm});
            skLineSegment(sketch, "E656", {"start": v(-1.73, 13.5) * mm, "end": v(-1.72, 13.45) * mm});
            skLineSegment(sketch, "E657", {"start": v(-1.72, 13.45) * mm, "end": v(-1.72, 13.43) * mm});
            skLineSegment(sketch, "E658", {"start": v(-1.72, 13.43) * mm, "end": v(-1.66, 12.95) * mm});
            skArc(sketch, "E659", {"start": v(-1.66, 12.95) * mm, "mid": v(-1.15, 13) * mm, "end": v(-0.63, 13.04) * mm});
            skLineSegment(sketch, "E660", {"start": v(-0.63, 13.04) * mm, "end": v(-0.66, 13.52) * mm});
            skLineSegment(sketch, "E661", {"start": v(-0.66, 13.52) * mm, "end": v(-0.66, 13.54) * mm});
            skLineSegment(sketch, "E662", {"start": v(-0.66, 13.54) * mm, "end": v(-0.66, 13.6) * mm});
            skLineSegment(sketch, "E663", {"start": v(-0.66, 13.6) * mm, "end": v(-0.65, 13.68) * mm});
            skLineSegment(sketch, "E664", {"start": v(-0.65, 13.68) * mm, "end": v(-0.63, 13.8) * mm});
            skLineSegment(sketch, "E665", {"start": v(-0.63, 13.8) * mm, "end": v(-0.6, 13.94) * mm});
            skLineSegment(sketch, "E666", {"start": v(-0.6, 13.94) * mm, "end": v(-0.57, 14.12) * mm});
            skLineSegment(sketch, "E667", {"start": v(-0.57, 14.12) * mm, "end": v(-0.5, 14.34) * mm});
            skLineSegment(sketch, "E668", {"start": v(-0.5, 14.34) * mm, "end": v(-0.42, 14.58) * mm});
            skLineSegment(sketch, "E669", {"start": v(-0.42, 14.58) * mm, "end": v(-0.34, 14.78) * mm});
            skArc(sketch, "E670", {"start": v(-0.34, 14.78) * mm, "mid": v(0.03, 14.79) * mm, "end": v(0.4, 14.78) * mm});
            skLineSegment(sketch, "E671", {"start": v(0.4, 14.78) * mm, "end": v(0.48, 14.58) * mm});
            skLineSegment(sketch, "E672", {"start": v(0.48, 14.58) * mm, "end": v(0.56, 14.33) * mm});
            skLineSegment(sketch, "E673", {"start": v(0.56, 14.33) * mm, "end": v(0.62, 14.12) * mm});
            skLineSegment(sketch, "E674", {"start": v(0.62, 14.12) * mm, "end": v(0.66, 13.94) * mm});
            skLineSegment(sketch, "E675", {"start": v(0.66, 13.94) * mm, "end": v(0.69, 13.8) * mm});
            skLineSegment(sketch, "E676", {"start": v(0.69, 13.8) * mm, "end": v(0.7, 13.67) * mm});
            skLineSegment(sketch, "E677", {"start": v(0.7, 13.67) * mm, "end": v(0.7, 13.59) * mm});
            skLineSegment(sketch, "E678", {"start": v(0.7, 13.59) * mm, "end": v(0.71, 13.54) * mm});
            skLineSegment(sketch, "E679", {"start": v(0.71, 13.54) * mm, "end": v(0.71, 13.52) * mm});
            skLineSegment(sketch, "E680", {"start": v(0.71, 13.52) * mm, "end": v(0.69, 13.04) * mm});
            skArc(sketch, "E681", {"start": v(0.69, 13.04) * mm, "mid": v(1.2, 13) * mm, "end": v(1.7, 12.95) * mm});
            skLineSegment(sketch, "E682", {"start": v(1.7, 12.95) * mm, "end": v(1.77, 13.42) * mm});
            skLineSegment(sketch, "E683", {"start": v(1.77, 13.42) * mm, "end": v(1.77, 13.44) * mm});
            skLineSegment(sketch, "E684", {"start": v(1.77, 13.44) * mm, "end": v(1.78, 13.49) * mm});
            skLineSegment(sketch, "E685", {"start": v(1.78, 13.49) * mm, "end": v(1.8, 13.57) * mm});
            skLineSegment(sketch, "E686", {"start": v(1.8, 13.57) * mm, "end": v(1.84, 13.68) * mm});
            skLineSegment(sketch, "E687", {"start": v(1.84, 13.68) * mm, "end": v(1.9, 13.83) * mm});
            skLineSegment(sketch, "E688", {"start": v(1.9, 13.83) * mm, "end": v(1.97, 14) * mm});
            skLineSegment(sketch, "E689", {"start": v(1.97, 14) * mm, "end": v(2.07, 14.2) * mm});
            skLineSegment(sketch, "E690", {"start": v(2.07, 14.2) * mm, "end": v(2.19, 14.42) * mm});
            skLineSegment(sketch, "E691", {"start": v(2.19, 14.42) * mm, "end": v(2.3, 14.6) * mm});
            skArc(sketch, "E692", {"start": v(2.3, 14.6) * mm, "mid": v(2.67, 14.54) * mm, "end": v(3.04, 14.47) * mm});
            skLineSegment(sketch, "E693", {"start": v(3.04, 14.47) * mm, "end": v(3.08, 14.26) * mm});
            skLineSegment(sketch, "E694", {"start": v(3.08, 14.26) * mm, "end": v(3.11, 14) * mm});
            skLineSegment(sketch, "E695", {"start": v(3.11, 14) * mm, "end": v(3.14, 13.78) * mm});
            skLineSegment(sketch, "E696", {"start": v(3.14, 13.78) * mm, "end": v(3.14, 13.6) * mm});
            skLineSegment(sketch, "E697", {"start": v(3.14, 13.6) * mm, "end": v(3.14, 13.45) * mm});
            skLineSegment(sketch, "E698", {"start": v(3.14, 13.45) * mm, "end": v(3.14, 13.33) * mm});
            skLineSegment(sketch, "E699", {"start": v(3.14, 13.33) * mm, "end": v(3.13, 13.24) * mm});
            skLineSegment(sketch, "E700", {"start": v(3.13, 13.24) * mm, "end": v(3.12, 13.2) * mm});
            skLineSegment(sketch, "E701", {"start": v(3.12, 13.2) * mm, "end": v(3.12, 13.18) * mm});
            skLineSegment(sketch, "E702", {"start": v(3.12, 13.18) * mm, "end": v(3, 12.7) * mm});
            skArc(sketch, "E703", {"start": v(3, 12.7) * mm, "mid": v(3.5, 12.58) * mm, "end": v(4, 12.43) * mm});
            skLineSegment(sketch, "E704", {"start": v(4, 12.43) * mm, "end": v(4.14, 12.9) * mm});
            skLineSegment(sketch, "E705", {"start": v(4.14, 12.9) * mm, "end": v(4.15, 12.9) * mm});
            skLineSegment(sketch, "E706", {"start": v(4.15, 12.9) * mm, "end": v(4.17, 12.95) * mm});
            skLineSegment(sketch, "E707", {"start": v(4.17, 12.95) * mm, "end": v(4.2, 13.03) * mm});
            skLineSegment(sketch, "E708", {"start": v(4.2, 13.03) * mm, "end": v(4.26, 13.14) * mm});
            skLineSegment(sketch, "E709", {"start": v(4.26, 13.14) * mm, "end": v(4.34, 13.27) * mm});
            skLineSegment(sketch, "E710", {"start": v(4.34, 13.27) * mm, "end": v(4.44, 13.42) * mm});
            skLineSegment(sketch, "E711", {"start": v(4.44, 13.42) * mm, "end": v(4.57, 13.6) * mm});
            skLineSegment(sketch, "E712", {"start": v(4.57, 13.6) * mm, "end": v(4.73, 13.8) * mm});
            skLineSegment(sketch, "E713", {"start": v(4.73, 13.8) * mm, "end": v(4.88, 13.96) * mm});
            skArc(sketch, "E714", {"start": v(4.88, 13.96) * mm, "mid": v(5.23, 13.83) * mm, "end": v(5.57, 13.7) * mm});
            skLineSegment(sketch, "E715", {"start": v(5.57, 13.7) * mm, "end": v(5.58, 13.48) * mm});
            skLineSegment(sketch, "E716", {"start": v(5.58, 13.48) * mm, "end": v(5.57, 13.22) * mm});
            skLineSegment(sketch, "E717", {"start": v(5.57, 13.22) * mm, "end": v(5.55, 13) * mm});
            skLineSegment(sketch, "E718", {"start": v(5.55, 13) * mm, "end": v(5.52, 12.82) * mm});
            skLineSegment(sketch, "E719", {"start": v(5.52, 12.82) * mm, "end": v(5.5, 12.67) * mm});
            skLineSegment(sketch, "E720", {"start": v(5.5, 12.67) * mm, "end": v(5.47, 12.55) * mm});
            skLineSegment(sketch, "E721", {"start": v(5.47, 12.55) * mm, "end": v(5.44, 12.47) * mm});
            skLineSegment(sketch, "E722", {"start": v(5.44, 12.47) * mm, "end": v(5.43, 12.42) * mm});
            skLineSegment(sketch, "E723", {"start": v(5.43, 12.42) * mm, "end": v(5.42, 12.4) * mm});
            skLineSegment(sketch, "E724", {"start": v(5.42, 12.4) * mm, "end": v(5.23, 11.97) * mm});
            skArc(sketch, "E725", {"start": v(5.23, 11.97) * mm, "mid": v(5.7, 11.75) * mm, "end": v(6.15, 11.52) * mm});
            skLineSegment(sketch, "E726", {"start": v(6.15, 11.52) * mm, "end": v(6.38, 11.94) * mm});
            skLineSegment(sketch, "E727", {"start": v(6.38, 11.94) * mm, "end": v(6.39, 11.96) * mm});
            skLineSegment(sketch, "E728", {"start": v(6.39, 11.96) * mm, "end": v(6.42, 12) * mm});
            skLineSegment(sketch, "E729", {"start": v(6.42, 12) * mm, "end": v(6.46, 12.07) * mm});
            skLineSegment(sketch, "E730", {"start": v(6.46, 12.07) * mm, "end": v(6.54, 12.16) * mm});
            skLineSegment(sketch, "E731", {"start": v(6.54, 12.16) * mm, "end": v(6.64, 12.28) * mm});
            skLineSegment(sketch, "E732", {"start": v(6.64, 12.28) * mm, "end": v(6.77, 12.41) * mm});
            skLineSegment(sketch, "E733", {"start": v(6.77, 12.41) * mm, "end": v(6.93, 12.56) * mm});
            skLineSegment(sketch, "E734", {"start": v(6.93, 12.56) * mm, "end": v(7.12, 12.73) * mm});
            skLineSegment(sketch, "E735", {"start": v(7.12, 12.73) * mm, "end": v(7.3, 12.86) * mm});
            skArc(sketch, "E736", {"start": v(7.3, 12.86) * mm, "mid": v(7.62, 12.68) * mm, "end": v(7.93, 12.48) * mm});
            skLineSegment(sketch, "E737", {"start": v(7.93, 12.48) * mm, "end": v(7.9, 12.26) * mm});
            skLineSegment(sketch, "E738", {"start": v(7.9, 12.26) * mm, "end": v(7.84, 12.02) * mm});
            skLineSegment(sketch, "E739", {"start": v(7.84, 12.02) * mm, "end": v(7.78, 11.8) * mm});
            skLineSegment(sketch, "E740", {"start": v(7.78, 11.8) * mm, "end": v(7.73, 11.63) * mm});
            skLineSegment(sketch, "E741", {"start": v(7.73, 11.63) * mm, "end": v(7.67, 11.48) * mm});
            skLineSegment(sketch, "E742", {"start": v(7.67, 11.48) * mm, "end": v(7.62, 11.38) * mm});
            skLineSegment(sketch, "E743", {"start": v(7.62, 11.38) * mm, "end": v(7.59, 11.3) * mm});
            skLineSegment(sketch, "E744", {"start": v(7.59, 11.3) * mm, "end": v(7.56, 11.26) * mm});
            skLineSegment(sketch, "E745", {"start": v(7.56, 11.26) * mm, "end": v(7.55, 11.24) * mm});
            skLineSegment(sketch, "E746", {"start": v(7.55, 11.24) * mm, "end": v(7.29, 10.84) * mm});
            skArc(sketch, "E747", {"start": v(7.29, 10.84) * mm, "mid": v(7.7, 10.55) * mm, "end": v(8.11, 10.24) * mm});
            skLineSegment(sketch, "E748", {"start": v(8.11, 10.24) * mm, "end": v(8.41, 10.61) * mm});
            skLineSegment(sketch, "E749", {"start": v(8.41, 10.61) * mm, "end": v(8.42, 10.63) * mm});
            skLineSegment(sketch, "E750", {"start": v(8.42, 10.63) * mm, "end": v(8.46, 10.66) * mm});
            skLineSegment(sketch, "E751", {"start": v(8.46, 10.66) * mm, "end": v(8.52, 10.72) * mm});
            skLineSegment(sketch, "E752", {"start": v(8.52, 10.72) * mm, "end": v(8.6, 10.8) * mm});
            skLineSegment(sketch, "E753", {"start": v(8.6, 10.8) * mm, "end": v(8.73, 10.9) * mm});
            skLineSegment(sketch, "E754", {"start": v(8.73, 10.9) * mm, "end": v(8.88, 11) * mm});
            skLineSegment(sketch, "E755", {"start": v(8.88, 11) * mm, "end": v(9.06, 11.13) * mm});
            skLineSegment(sketch, "E756", {"start": v(9.06, 11.13) * mm, "end": v(9.28, 11.25) * mm});
            skLineSegment(sketch, "E757", {"start": v(9.28, 11.25) * mm, "end": v(9.48, 11.35) * mm});
            skArc(sketch, "E758", {"start": v(9.48, 11.35) * mm, "mid": v(9.76, 11.11) * mm, "end": v(10.04, 10.86) * mm});
            skLineSegment(sketch, "E759", {"start": v(10.04, 10.86) * mm, "end": v(9.96, 10.66) * mm});
            skLineSegment(sketch, "E760", {"start": v(9.96, 10.66) * mm, "end": v(9.86, 10.42) * mm});
            skLineSegment(sketch, "E761", {"start": v(9.86, 10.42) * mm, "end": v(9.77, 10.22) * mm});
            skLineSegment(sketch, "E762", {"start": v(9.77, 10.22) * mm, "end": v(9.68, 10.06) * mm});
            skLineSegment(sketch, "E763", {"start": v(9.68, 10.06) * mm, "end": v(9.6, 9.93) * mm});
            skLineSegment(sketch, "E764", {"start": v(9.6, 9.93) * mm, "end": v(9.54, 9.83) * mm});
            skLineSegment(sketch, "E765", {"start": v(9.54, 9.83) * mm, "end": v(9.48, 9.76) * mm});
            skLineSegment(sketch, "E766", {"start": v(9.48, 9.76) * mm, "end": v(9.45, 9.72) * mm});
            skLineSegment(sketch, "E767", {"start": v(9.45, 9.72) * mm, "end": v(9.44, 9.71) * mm});
            skLineSegment(sketch, "E768", {"start": v(9.44, 9.71) * mm, "end": v(9.1, 9.37) * mm});
            skArc(sketch, "E769", {"start": v(9.1, 9.37) * mm, "mid": v(9.47, 9) * mm, "end": v(9.81, 8.62) * mm});
            skLineSegment(sketch, "E770", {"start": v(3.7, 4.02) * mm, "end": v(4.19, 4.55) * mm});
            skLineSegment(sketch, "E771", {"start": v(4.19, 4.55) * mm, "end": v(4.2, 4.56) * mm});
            skLineSegment(sketch, "E772", {"start": v(4.2, 4.56) * mm, "end": v(4.21, 4.57) * mm});
            skLineSegment(sketch, "E773", {"start": v(4.21, 4.57) * mm, "end": v(4.24, 4.6) * mm});
            skLineSegment(sketch, "E774", {"start": v(4.24, 4.6) * mm, "end": v(4.28, 4.63) * mm});
            skLineSegment(sketch, "E775", {"start": v(4.28, 4.63) * mm, "end": v(4.34, 4.67) * mm});
            skLineSegment(sketch, "E776", {"start": v(4.34, 4.67) * mm, "end": v(4.41, 4.71) * mm});
            skLineSegment(sketch, "E777", {"start": v(4.41, 4.71) * mm, "end": v(4.5, 4.76) * mm});
            skLineSegment(sketch, "E778", {"start": v(4.5, 4.76) * mm, "end": v(4.6, 4.81) * mm});
            skLineSegment(sketch, "E779", {"start": v(4.6, 4.81) * mm, "end": v(4.73, 4.87) * mm});
            skLineSegment(sketch, "E780", {"start": v(4.73, 4.87) * mm, "end": v(4.87, 4.92) * mm});
            skLineSegment(sketch, "E781", {"start": v(4.87, 4.92) * mm, "end": v(5.02, 4.96) * mm});
            skLineSegment(sketch, "E782", {"start": v(5.02, 4.96) * mm, "end": v(5.17, 5) * mm});
            skArc(sketch, "E783", {"start": v(5.17, 5) * mm, "mid": v(5.4, 4.76) * mm, "end": v(5.6, 4.5) * mm});
            skLineSegment(sketch, "E784", {"start": v(5.6, 4.5) * mm, "end": v(5.55, 4.37) * mm});
            skLineSegment(sketch, "E785", {"start": v(5.55, 4.37) * mm, "end": v(5.49, 4.22) * mm});
            skLineSegment(sketch, "E786", {"start": v(5.49, 4.22) * mm, "end": v(5.42, 4.09) * mm});
            skLineSegment(sketch, "E787", {"start": v(5.42, 4.09) * mm, "end": v(5.35, 3.97) * mm});
            skLineSegment(sketch, "E788", {"start": v(5.35, 3.97) * mm, "end": v(5.29, 3.87) * mm});
            skLineSegment(sketch, "E789", {"start": v(5.29, 3.87) * mm, "end": v(5.23, 3.8) * mm});
            skLineSegment(sketch, "E790", {"start": v(5.23, 3.8) * mm, "end": v(5.18, 3.73) * mm});
            skLineSegment(sketch, "E791", {"start": v(5.18, 3.73) * mm, "end": v(5.13, 3.67) * mm});
            skLineSegment(sketch, "E792", {"start": v(5.13, 3.67) * mm, "end": v(5.1, 3.64) * mm});
            skLineSegment(sketch, "E793", {"start": v(5.1, 3.64) * mm, "end": v(5.06, 3.6) * mm});
            skLineSegment(sketch, "E794", {"start": v(5.06, 3.6) * mm, "end": v(5.05, 3.6) * mm});
            skLineSegment(sketch, "E795", {"start": v(5.05, 3.6) * mm, "end": v(5.04, 3.59) * mm});
            skLineSegment(sketch, "E796", {"start": v(5.04, 3.59) * mm, "end": v(4.45, 3.17) * mm});
            skArc(sketch, "E797", {"start": v(4.45, 3.17) * mm, "mid": v(4.73, 2.74) * mm, "end": v(4.96, 2.3) * mm});
            skLineSegment(sketch, "E798", {"start": v(4.96, 2.3) * mm, "end": v(5.62, 2.6) * mm});
            skLineSegment(sketch, "E799", {"start": v(5.62, 2.6) * mm, "end": v(5.63, 2.6) * mm});
            skLineSegment(sketch, "E800", {"start": v(5.63, 2.6) * mm, "end": v(5.65, 2.61) * mm});
            skLineSegment(sketch, "E801", {"start": v(5.65, 2.61) * mm, "end": v(5.68, 2.62) * mm});
            skLineSegment(sketch, "E802", {"start": v(5.68, 2.62) * mm, "end": v(5.74, 2.64) * mm});
            skLineSegment(sketch, "E803", {"start": v(5.74, 2.64) * mm, "end": v(5.8, 2.65) * mm});
            skLineSegment(sketch, "E804", {"start": v(5.8, 2.65) * mm, "end": v(5.89, 2.67) * mm});
            skLineSegment(sketch, "E805", {"start": v(5.89, 2.67) * mm, "end": v(5.99, 2.68) * mm});
            skLineSegment(sketch, "E806", {"start": v(5.99, 2.68) * mm, "end": v(6.1, 2.68) * mm});
            skLineSegment(sketch, "E807", {"start": v(6.1, 2.68) * mm, "end": v(6.24, 2.68) * mm});
            skLineSegment(sketch, "E808", {"start": v(6.24, 2.68) * mm, "end": v(6.38, 2.68) * mm});
            skLineSegment(sketch, "E809", {"start": v(6.38, 2.68) * mm, "end": v(6.55, 2.66) * mm});
            skLineSegment(sketch, "E810", {"start": v(6.55, 2.66) * mm, "end": v(6.7, 2.64) * mm});
            skArc(sketch, "E811", {"start": v(6.7, 2.64) * mm, "mid": v(6.8, 2.33) * mm, "end": v(6.9, 2.01) * mm});
            skLineSegment(sketch, "E812", {"start": v(6.9, 2.01) * mm, "end": v(6.8, 1.9) * mm});
            skLineSegment(sketch, "E813", {"start": v(6.8, 1.9) * mm, "end": v(6.69, 1.8) * mm});
            skLineSegment(sketch, "E814", {"start": v(6.69, 1.8) * mm, "end": v(6.58, 1.7) * mm});
            skLineSegment(sketch, "E815", {"start": v(6.58, 1.7) * mm, "end": v(6.47, 1.62) * mm});
            skLineSegment(sketch, "E816", {"start": v(6.47, 1.62) * mm, "end": v(6.37, 1.55) * mm});
            skLineSegment(sketch, "E817", {"start": v(6.37, 1.55) * mm, "end": v(6.29, 1.5) * mm});
            skLineSegment(sketch, "E818", {"start": v(6.29, 1.5) * mm, "end": v(6.21, 1.46) * mm});
            skLineSegment(sketch, "E819", {"start": v(6.21, 1.46) * mm, "end": v(6.15, 1.43) * mm});
            skLineSegment(sketch, "E820", {"start": v(6.15, 1.43) * mm, "end": v(6.1, 1.4) * mm});
            skLineSegment(sketch, "E821", {"start": v(6.1, 1.4) * mm, "end": v(6.07, 1.4) * mm});
            skLineSegment(sketch, "E822", {"start": v(6.07, 1.4) * mm, "end": v(6.04, 1.39) * mm});
            skLineSegment(sketch, "E823", {"start": v(6.04, 1.39) * mm, "end": v(6.04, 1.39) * mm});
            skLineSegment(sketch, "E824", {"start": v(6.04, 1.39) * mm, "end": v(5.33, 1.22) * mm});
            skArc(sketch, "E825", {"start": v(5.33, 1.22) * mm, "mid": v(5.42, 0.73) * mm, "end": v(5.47, 0.22) * mm});
            skLineSegment(sketch, "E826", {"start": v(5.47, 0.22) * mm, "end": v(6.2, 0.25) * mm});
            skLineSegment(sketch, "E827", {"start": v(6.2, 0.25) * mm, "end": v(6.2, 0.25) * mm});
            skLineSegment(sketch, "E828", {"start": v(6.2, 0.25) * mm, "end": v(6.22, 0.25) * mm});
            skLineSegment(sketch, "E829", {"start": v(6.22, 0.25) * mm, "end": v(6.26, 0.25) * mm});
            skLineSegment(sketch, "E830", {"start": v(6.26, 0.25) * mm, "end": v(6.31, 0.24) * mm});
            skLineSegment(sketch, "E831", {"start": v(6.31, 0.24) * mm, "end": v(6.38, 0.23) * mm});
            skLineSegment(sketch, "E832", {"start": v(6.38, 0.23) * mm, "end": v(6.47, 0.2) * mm});
            skLineSegment(sketch, "E833", {"start": v(6.47, 0.2) * mm, "end": v(6.56, 0.18) * mm});
            skLineSegment(sketch, "E834", {"start": v(6.56, 0.18) * mm, "end": v(6.67, 0.14) * mm});
            skLineSegment(sketch, "E835", {"start": v(6.67, 0.14) * mm, "end": v(6.8, 0.1) * mm});
            skLineSegment(sketch, "E836", {"start": v(6.8, 0.1) * mm, "end": v(6.93, 0.03) * mm});
            skLineSegment(sketch, "E837", {"start": v(6.93, 0.03) * mm, "end": v(7.07, -0.04) * mm});
            skLineSegment(sketch, "E838", {"start": v(7.07, -0.04) * mm, "end": v(7.2, -0.12) * mm});
            skArc(sketch, "E839", {"start": v(7.2, -0.12) * mm, "mid": v(7.19, -0.45) * mm, "end": v(7.16, -0.78) * mm});
            skLineSegment(sketch, "E840", {"start": v(7.16, -0.78) * mm, "end": v(7.02, -0.84) * mm});
            skLineSegment(sketch, "E841", {"start": v(7.02, -0.84) * mm, "end": v(6.87, -0.9) * mm});
            skLineSegment(sketch, "E842", {"start": v(6.87, -0.9) * mm, "end": v(6.73, -0.95) * mm});
            skLineSegment(sketch, "E843", {"start": v(6.73, -0.95) * mm, "end": v(6.6, -0.98) * mm});
            skLineSegment(sketch, "E844", {"start": v(6.6, -0.98) * mm, "end": v(6.5, -1) * mm});
            skLineSegment(sketch, "E845", {"start": v(6.5, -1) * mm, "end": v(6.4, -1.02) * mm});
            skLineSegment(sketch, "E846", {"start": v(6.4, -1.02) * mm, "end": v(6.3, -1.03) * mm});
            skLineSegment(sketch, "E847", {"start": v(6.3, -1.03) * mm, "end": v(6.24, -1.03) * mm});
            skLineSegment(sketch, "E848", {"start": v(6.24, -1.03) * mm, "end": v(6.18, -1.03) * mm});
            skLineSegment(sketch, "E849", {"start": v(6.18, -1.03) * mm, "end": v(6.14, -1.03) * mm});
            skLineSegment(sketch, "E850", {"start": v(6.14, -1.03) * mm, "end": v(6.12, -1.03) * mm});
            skLineSegment(sketch, "E851", {"start": v(6.12, -1.03) * mm, "end": v(6.11, -1.03) * mm});
            skLineSegment(sketch, "E852", {"start": v(6.11, -1.03) * mm, "end": v(5.4, -0.91) * mm});
            skArc(sketch, "E853", {"start": v(5.4, -0.91) * mm, "mid": v(5.3, -1.4) * mm, "end": v(5.14, -1.9) * mm});
            skLineSegment(sketch, "E854", {"start": v(5.14, -1.9) * mm, "end": v(5.82, -2.14) * mm});
            skLineSegment(sketch, "E855", {"start": v(5.82, -2.14) * mm, "end": v(5.83, -2.14) * mm});
            skLineSegment(sketch, "E856", {"start": v(5.83, -2.14) * mm, "end": v(5.85, -2.15) * mm});
            skLineSegment(sketch, "E857", {"start": v(5.85, -2.15) * mm, "end": v(5.88, -2.17) * mm});
            skLineSegment(sketch, "E858", {"start": v(5.88, -2.17) * mm, "end": v(5.93, -2.2) * mm});
            skLineSegment(sketch, "E859", {"start": v(5.93, -2.2) * mm, "end": v(5.99, -2.23) * mm});
            skLineSegment(sketch, "E860", {"start": v(5.99, -2.23) * mm, "end": v(6.06, -2.28) * mm});
            skLineSegment(sketch, "E861", {"start": v(6.06, -2.28) * mm, "end": v(6.14, -2.35) * mm});
            skLineSegment(sketch, "E862", {"start": v(6.14, -2.35) * mm, "end": v(6.22, -2.42) * mm});
            skLineSegment(sketch, "E863", {"start": v(6.22, -2.42) * mm, "end": v(6.32, -2.52) * mm});
            skLineSegment(sketch, "E864", {"start": v(6.32, -2.52) * mm, "end": v(6.42, -2.62) * mm});
            skLineSegment(sketch, "E865", {"start": v(6.42, -2.62) * mm, "end": v(6.52, -2.75) * mm});
            skLineSegment(sketch, "E866", {"start": v(6.52, -2.75) * mm, "end": v(6.61, -2.87) * mm});
            skArc(sketch, "E867", {"start": v(6.61, -2.87) * mm, "mid": v(6.47, -3.17) * mm, "end": v(6.32, -3.46) * mm});
            skLineSegment(sketch, "E868", {"start": v(6.32, -3.46) * mm, "end": v(6.17, -3.47) * mm});
            skLineSegment(sketch, "E869", {"start": v(6.17, -3.47) * mm, "end": v(6, -3.46) * mm});
            skLineSegment(sketch, "E870", {"start": v(6, -3.46) * mm, "end": v(5.86, -3.45) * mm});
            skLineSegment(sketch, "E871", {"start": v(5.86, -3.45) * mm, "end": v(5.73, -3.43) * mm});
            skLineSegment(sketch, "E872", {"start": v(5.73, -3.43) * mm, "end": v(5.62, -3.41) * mm});
            skLineSegment(sketch, "E873", {"start": v(5.62, -3.41) * mm, "end": v(5.52, -3.39) * mm});
            skLineSegment(sketch, "E874", {"start": v(5.52, -3.39) * mm, "end": v(5.44, -3.37) * mm});
            skLineSegment(sketch, "E875", {"start": v(5.44, -3.37) * mm, "end": v(5.37, -3.34) * mm});
            skLineSegment(sketch, "E876", {"start": v(5.37, -3.34) * mm, "end": v(5.32, -3.32) * mm});
            skLineSegment(sketch, "E877", {"start": v(5.32, -3.32) * mm, "end": v(5.29, -3.3) * mm});
            skLineSegment(sketch, "E878", {"start": v(5.29, -3.3) * mm, "end": v(5.27, -3.3) * mm});
            skLineSegment(sketch, "E879", {"start": v(5.27, -3.3) * mm, "end": v(5.26, -3.3) * mm});
            skLineSegment(sketch, "E880", {"start": v(5.26, -3.3) * mm, "end": v(4.65, -2.9) * mm});
            skArc(sketch, "E881", {"start": v(4.65, -2.9) * mm, "mid": v(4.36, -3.33) * mm, "end": v(4.03, -3.72) * mm});
            skLineSegment(sketch, "E882", {"start": v(4.03, -3.72) * mm, "end": v(4.57, -4.2) * mm});
            skLineSegment(sketch, "E883", {"start": v(4.57, -4.2) * mm, "end": v(4.57, -4.2) * mm});
            skLineSegment(sketch, "E884", {"start": v(4.57, -4.2) * mm, "end": v(4.59, -4.23) * mm});
            skLineSegment(sketch, "E885", {"start": v(4.59, -4.23) * mm, "end": v(4.61, -4.26) * mm});
            skLineSegment(sketch, "E886", {"start": v(4.61, -4.26) * mm, "end": v(4.65, -4.3) * mm});
            skLineSegment(sketch, "E887", {"start": v(4.65, -4.3) * mm, "end": v(4.68, -4.36) * mm});
            skLineSegment(sketch, "E888", {"start": v(4.68, -4.36) * mm, "end": v(4.73, -4.43) * mm});
            skLineSegment(sketch, "E889", {"start": v(4.73, -4.43) * mm, "end": v(4.78, -4.52) * mm});
            skLineSegment(sketch, "E890", {"start": v(4.78, -4.52) * mm, "end": v(4.83, -4.62) * mm});
            skLineSegment(sketch, "E891", {"start": v(4.83, -4.62) * mm, "end": v(4.88, -4.74) * mm});
            skLineSegment(sketch, "E892", {"start": v(4.88, -4.74) * mm, "end": v(4.93, -4.88) * mm});
            skLineSegment(sketch, "E893", {"start": v(4.93, -4.88) * mm, "end": v(4.98, -5.04) * mm});
            skLineSegment(sketch, "E894", {"start": v(4.98, -5.04) * mm, "end": v(5.02, -5.18) * mm});
            skArc(sketch, "E895", {"start": v(5.02, -5.18) * mm, "mid": v(4.77, -5.4) * mm, "end": v(4.52, -5.62) * mm});
            skLineSegment(sketch, "E896", {"start": v(4.52, -5.62) * mm, "end": v(4.38, -5.57) * mm});
            skLineSegment(sketch, "E897", {"start": v(4.38, -5.57) * mm, "end": v(4.23, -5.5) * mm});
            skLineSegment(sketch, "E898", {"start": v(4.23, -5.5) * mm, "end": v(4.1, -5.43) * mm});
            skLineSegment(sketch, "E899", {"start": v(4.1, -5.43) * mm, "end": v(3.99, -5.37) * mm});
            skLineSegment(sketch, "E900", {"start": v(3.99, -5.37) * mm, "end": v(3.89, -5.3) * mm});
            skLineSegment(sketch, "E901", {"start": v(3.89, -5.3) * mm, "end": v(3.8, -5.24) * mm});
            skLineSegment(sketch, "E902", {"start": v(3.8, -5.24) * mm, "end": v(3.74, -5.2) * mm});
            skLineSegment(sketch, "E903", {"start": v(3.74, -5.2) * mm, "end": v(3.69, -5.14) * mm});
            skLineSegment(sketch, "E904", {"start": v(3.69, -5.14) * mm, "end": v(3.65, -5.1) * mm});
            skLineSegment(sketch, "E905", {"start": v(3.65, -5.1) * mm, "end": v(3.62, -5.08) * mm});
            skLineSegment(sketch, "E906", {"start": v(3.62, -5.08) * mm, "end": v(3.6, -5.06) * mm});
            skLineSegment(sketch, "E907", {"start": v(3.6, -5.06) * mm, "end": v(3.6, -5.05) * mm});
            skLineSegment(sketch, "E908", {"start": v(3.6, -5.05) * mm, "end": v(3.18, -4.47) * mm});
            skArc(sketch, "E909", {"start": v(3.18, -4.47) * mm, "mid": v(2.76, -4.74) * mm, "end": v(2.31, -4.98) * mm});
            skLineSegment(sketch, "E910", {"start": v(2.31, -4.98) * mm, "end": v(2.62, -5.63) * mm});
            skLineSegment(sketch, "E911", {"start": v(2.62, -5.63) * mm, "end": v(2.62, -5.64) * mm});
            skLineSegment(sketch, "E912", {"start": v(2.62, -5.64) * mm, "end": v(2.63, -5.66) * mm});
            skLineSegment(sketch, "E913", {"start": v(2.63, -5.66) * mm, "end": v(2.64, -5.7) * mm});
            skLineSegment(sketch, "E914", {"start": v(2.64, -5.7) * mm, "end": v(2.65, -5.75) * mm});
            skLineSegment(sketch, "E915", {"start": v(2.65, -5.75) * mm, "end": v(2.67, -5.82) * mm});
            skLineSegment(sketch, "E916", {"start": v(2.67, -5.82) * mm, "end": v(2.68, -5.9) * mm});
            skLineSegment(sketch, "E917", {"start": v(2.68, -5.9) * mm, "end": v(2.7, -6) * mm});
            skLineSegment(sketch, "E918", {"start": v(2.7, -6) * mm, "end": v(2.7, -6.12) * mm});
            skLineSegment(sketch, "E919", {"start": v(2.7, -6.12) * mm, "end": v(2.7, -6.25) * mm});
            skLineSegment(sketch, "E920", {"start": v(2.7, -6.25) * mm, "end": v(2.7, -6.4) * mm});
            skLineSegment(sketch, "E921", {"start": v(2.7, -6.4) * mm, "end": v(2.68, -6.56) * mm});
            skLineSegment(sketch, "E922", {"start": v(2.68, -6.56) * mm, "end": v(2.66, -6.7) * mm});
            skArc(sketch, "E923", {"start": v(2.66, -6.7) * mm, "mid": v(2.35, -6.82) * mm, "end": v(2.03, -6.92) * mm});
            skLineSegment(sketch, "E924", {"start": v(2.03, -6.92) * mm, "end": v(1.92, -6.82) * mm});
            skLineSegment(sketch, "E925", {"start": v(1.92, -6.82) * mm, "end": v(1.81, -6.7) * mm});
            skLineSegment(sketch, "E926", {"start": v(1.81, -6.7) * mm, "end": v(1.72, -6.59) * mm});
            skLineSegment(sketch, "E927", {"start": v(1.72, -6.59) * mm, "end": v(1.64, -6.48) * mm});
            skLineSegment(sketch, "E928", {"start": v(1.64, -6.48) * mm, "end": v(1.57, -6.39) * mm});
            skLineSegment(sketch, "E929", {"start": v(1.57, -6.39) * mm, "end": v(1.52, -6.3) * mm});
            skLineSegment(sketch, "E930", {"start": v(1.52, -6.3) * mm, "end": v(1.48, -6.23) * mm});
            skLineSegment(sketch, "E931", {"start": v(1.48, -6.23) * mm, "end": v(1.45, -6.17) * mm});
            skLineSegment(sketch, "E932", {"start": v(1.45, -6.17) * mm, "end": v(1.42, -6.12) * mm});
            skLineSegment(sketch, "E933", {"start": v(1.42, -6.12) * mm, "end": v(1.41, -6.08) * mm});
            skLineSegment(sketch, "E934", {"start": v(1.41, -6.08) * mm, "end": v(1.4, -6.06) * mm});
            skLineSegment(sketch, "E935", {"start": v(1.4, -6.06) * mm, "end": v(1.4, -6.05) * mm});
            skLineSegment(sketch, "E936", {"start": v(1.4, -6.05) * mm, "end": v(1.24, -5.35) * mm});
            skArc(sketch, "E937", {"start": v(1.24, -5.35) * mm, "mid": v(0.74, -5.44) * mm, "end": v(0.24, -5.48) * mm});
            skLineSegment(sketch, "E938", {"start": v(0.24, -5.48) * mm, "end": v(0.27, -6.2) * mm});
            skLineSegment(sketch, "E939", {"start": v(0.27, -6.2) * mm, "end": v(0.27, -6.21) * mm});
            skLineSegment(sketch, "E940", {"start": v(0.27, -6.21) * mm, "end": v(0.27, -6.24) * mm});
            skLineSegment(sketch, "E941", {"start": v(0.27, -6.24) * mm, "end": v(0.26, -6.27) * mm});
            skLineSegment(sketch, "E942", {"start": v(0.26, -6.27) * mm, "end": v(0.26, -6.33) * mm});
            skLineSegment(sketch, "E943", {"start": v(0.26, -6.33) * mm, "end": v(0.24, -6.4) * mm});
            skLineSegment(sketch, "E944", {"start": v(0.24, -6.4) * mm, "end": v(0.22, -6.48) * mm});
            skLineSegment(sketch, "E945", {"start": v(0.22, -6.48) * mm, "end": v(0.2, -6.58) * mm});
            skLineSegment(sketch, "E946", {"start": v(0.2, -6.58) * mm, "end": v(0.16, -6.69) * mm});
            skLineSegment(sketch, "E947", {"start": v(0.16, -6.69) * mm, "end": v(0.1, -6.8) * mm});
            skLineSegment(sketch, "E948", {"start": v(0.1, -6.8) * mm, "end": v(0.05, -6.94) * mm});
            skLineSegment(sketch, "E949", {"start": v(0.05, -6.94) * mm, "end": v(-0.03, -7.09) * mm});
            skLineSegment(sketch, "E950", {"start": v(-0.03, -7.09) * mm, "end": v(-0.1, -7.21) * mm});
            skArc(sketch, "E951", {"start": v(-0.1, -7.21) * mm, "mid": v(-0.44, -7.2) * mm, "end": v(-0.77, -7.17) * mm});
            skLineSegment(sketch, "E952", {"start": v(-0.77, -7.17) * mm, "end": v(-0.83, -7.04) * mm});
            skLineSegment(sketch, "E953", {"start": v(-0.83, -7.04) * mm, "end": v(-0.89, -6.89) * mm});
            skLineSegment(sketch, "E954", {"start": v(-0.89, -6.89) * mm, "end": v(-0.93, -6.75) * mm});
            skLineSegment(sketch, "E955", {"start": v(-0.93, -6.75) * mm, "end": v(-0.96, -6.62) * mm});
            skLineSegment(sketch, "E956", {"start": v(-0.96, -6.62) * mm, "end": v(-0.99, -6.5) * mm});
            skLineSegment(sketch, "E957", {"start": v(-0.99, -6.5) * mm, "end": v(-1, -6.4) * mm});
            skLineSegment(sketch, "E958", {"start": v(-1, -6.4) * mm, "end": v(-1.01, -6.32) * mm});
            skLineSegment(sketch, "E959", {"start": v(-1.01, -6.32) * mm, "end": v(-1.02, -6.25) * mm});
            skLineSegment(sketch, "E960", {"start": v(-1.02, -6.25) * mm, "end": v(-1.02, -6.2) * mm});
            skLineSegment(sketch, "E961", {"start": v(-1.02, -6.2) * mm, "end": v(-1.02, -6.16) * mm});
            skLineSegment(sketch, "E962", {"start": v(-1.02, -6.16) * mm, "end": v(-1.02, -6.13) * mm});
            skLineSegment(sketch, "E963", {"start": v(-1.02, -6.13) * mm, "end": v(-1.01, -6.13) * mm});
            skLineSegment(sketch, "E964", {"start": v(-1.01, -6.13) * mm, "end": v(-0.9, -5.41) * mm});
            skArc(sketch, "E965", {"start": v(-0.9, -5.41) * mm, "mid": v(-1.4, -5.3) * mm, "end": v(-1.88, -5.16) * mm});
            skLineSegment(sketch, "E966", {"start": v(-1.88, -5.16) * mm, "end": v(-2.12, -5.84) * mm});
            skLineSegment(sketch, "E967", {"start": v(-2.12, -5.84) * mm, "end": v(-2.13, -5.84) * mm});
            skLineSegment(sketch, "E968", {"start": v(-2.13, -5.84) * mm, "end": v(-2.14, -5.86) * mm});
            skLineSegment(sketch, "E969", {"start": v(-2.14, -5.86) * mm, "end": v(-2.15, -5.9) * mm});
            skLineSegment(sketch, "E970", {"start": v(-2.15, -5.9) * mm, "end": v(-2.18, -5.95) * mm});
            skLineSegment(sketch, "E971", {"start": v(-2.18, -5.95) * mm, "end": v(-2.22, -6) * mm});
            skLineSegment(sketch, "E972", {"start": v(-2.22, -6) * mm, "end": v(-2.27, -6.07) * mm});
            skLineSegment(sketch, "E973", {"start": v(-2.27, -6.07) * mm, "end": v(-2.33, -6.15) * mm});
            skLineSegment(sketch, "E974", {"start": v(-2.33, -6.15) * mm, "end": v(-2.4, -6.24) * mm});
            skLineSegment(sketch, "E975", {"start": v(-2.4, -6.24) * mm, "end": v(-2.5, -6.33) * mm});
            skLineSegment(sketch, "E976", {"start": v(-2.5, -6.33) * mm, "end": v(-2.6, -6.43) * mm});
            skLineSegment(sketch, "E977", {"start": v(-2.6, -6.43) * mm, "end": v(-2.73, -6.54) * mm});
            skLineSegment(sketch, "E978", {"start": v(-2.73, -6.54) * mm, "end": v(-2.85, -6.63) * mm});
            skArc(sketch, "E979", {"start": v(-2.85, -6.63) * mm, "mid": v(-3.15, -6.49) * mm, "end": v(-3.45, -6.33) * mm});
            skLineSegment(sketch, "E980", {"start": v(-3.45, -6.33) * mm, "end": v(-3.45, -6.19) * mm});
            skLineSegment(sketch, "E981", {"start": v(-3.45, -6.19) * mm, "end": v(-3.45, -6.02) * mm});
            skLineSegment(sketch, "E982", {"start": v(-3.45, -6.02) * mm, "end": v(-3.44, -5.88) * mm});
            skLineSegment(sketch, "E983", {"start": v(-3.44, -5.88) * mm, "end": v(-3.42, -5.75) * mm});
            skLineSegment(sketch, "E984", {"start": v(-3.42, -5.75) * mm, "end": v(-3.4, -5.63) * mm});
            skLineSegment(sketch, "E985", {"start": v(-3.4, -5.63) * mm, "end": v(-3.37, -5.53) * mm});
            skLineSegment(sketch, "E986", {"start": v(-3.37, -5.53) * mm, "end": v(-3.35, -5.45) * mm});
            skLineSegment(sketch, "E987", {"start": v(-3.35, -5.45) * mm, "end": v(-3.33, -5.39) * mm});
            skLineSegment(sketch, "E988", {"start": v(-3.33, -5.39) * mm, "end": v(-3.3, -5.34) * mm});
            skLineSegment(sketch, "E989", {"start": v(-3.3, -5.34) * mm, "end": v(-3.3, -5.3) * mm});
            skLineSegment(sketch, "E990", {"start": v(-3.3, -5.3) * mm, "end": v(-3.28, -5.28) * mm});
            skLineSegment(sketch, "E991", {"start": v(-3.28, -5.28) * mm, "end": v(-3.28, -5.27) * mm});
            skLineSegment(sketch, "E992", {"start": v(-3.28, -5.27) * mm, "end": v(-2.9, -4.66) * mm});
            skArc(sketch, "E993", {"start": v(-2.9, -4.66) * mm, "mid": v(-3.31, -4.37) * mm, "end": v(-3.7, -4.05) * mm});
            skLineSegment(sketch, "E994", {"start": v(-3.7, -4.05) * mm, "end": v(-4.19, -4.58) * mm});
            skLineSegment(sketch, "E995", {"start": v(-4.19, -4.58) * mm, "end": v(-4.2, -4.59) * mm});
            skLineSegment(sketch, "E996", {"start": v(-4.2, -4.59) * mm, "end": v(-4.21, -4.6) * mm});
            skLineSegment(sketch, "E997", {"start": v(-4.21, -4.6) * mm, "end": v(-4.24, -4.63) * mm});
            skLineSegment(sketch, "E998", {"start": v(-4.24, -4.63) * mm, "end": v(-4.28, -4.66) * mm});
            skLineSegment(sketch, "E999", {"start": v(-4.28, -4.66) * mm, "end": v(-4.34, -4.7) * mm});
            skLineSegment(sketch, "E1000", {"start": v(-4.34, -4.7) * mm, "end": v(-4.41, -4.74) * mm});
            skLineSegment(sketch, "E1001", {"start": v(-4.41, -4.74) * mm, "end": v(-4.5, -4.8) * mm});
            skLineSegment(sketch, "E1002", {"start": v(-4.5, -4.8) * mm, "end": v(-4.6, -4.84) * mm});
            skLineSegment(sketch, "E1003", {"start": v(-4.6, -4.84) * mm, "end": v(-4.73, -4.9) * mm});
            skLineSegment(sketch, "E1004", {"start": v(-4.73, -4.9) * mm, "end": v(-4.87, -4.95) * mm});
            skLineSegment(sketch, "E1005", {"start": v(-4.87, -4.95) * mm, "end": v(-5.02, -5) * mm});
            skLineSegment(sketch, "E1006", {"start": v(-5.02, -5) * mm, "end": v(-5.16, -5.03) * mm});
            skArc(sketch, "E1007", {"start": v(-5.16, -5.03) * mm, "mid": v(-5.4, -4.79) * mm, "end": v(-5.6, -4.53) * mm});
            skLineSegment(sketch, "E1008", {"start": v(-5.6, -4.53) * mm, "end": v(-5.55, -4.4) * mm});
            skLineSegment(sketch, "E1009", {"start": v(-5.55, -4.4) * mm, "end": v(-5.48, -4.25) * mm});
            skLineSegment(sketch, "E1010", {"start": v(-5.48, -4.25) * mm, "end": v(-5.42, -4.12) * mm});
            skLineSegment(sketch, "E1011", {"start": v(-5.42, -4.12) * mm, "end": v(-5.35, -4) * mm});
            skLineSegment(sketch, "E1012", {"start": v(-5.35, -4) * mm, "end": v(-5.29, -3.9) * mm});
            skLineSegment(sketch, "E1013", {"start": v(-5.29, -3.9) * mm, "end": v(-5.23, -3.82) * mm});
            skLineSegment(sketch, "E1014", {"start": v(-5.23, -3.82) * mm, "end": v(-5.18, -3.76) * mm});
            skLineSegment(sketch, "E1015", {"start": v(-5.18, -3.76) * mm, "end": v(-5.13, -3.7) * mm});
            skLineSegment(sketch, "E1016", {"start": v(-5.13, -3.7) * mm, "end": v(-5.1, -3.66) * mm});
            skLineSegment(sketch, "E1017", {"start": v(-5.1, -3.66) * mm, "end": v(-5.06, -3.64) * mm});
            skLineSegment(sketch, "E1018", {"start": v(-5.06, -3.64) * mm, "end": v(-5.05, -3.62) * mm});
            skLineSegment(sketch, "E1019", {"start": v(-5.05, -3.62) * mm, "end": v(-5.04, -3.62) * mm});
            skLineSegment(sketch, "E1020", {"start": v(-5.04, -3.62) * mm, "end": v(-4.45, -3.2) * mm});
            skArc(sketch, "E1021", {"start": v(-4.45, -3.2) * mm, "mid": v(-4.73, -2.77) * mm, "end": v(-4.96, -2.32) * mm});
            skLineSegment(sketch, "E1022", {"start": v(-4.96, -2.32) * mm, "end": v(-5.62, -2.63) * mm});
            skLineSegment(sketch, "E1023", {"start": v(-5.62, -2.63) * mm, "end": v(-5.62, -2.63) * mm});
            skLineSegment(sketch, "E1024", {"start": v(-5.62, -2.63) * mm, "end": v(-5.65, -2.64) * mm});
            skLineSegment(sketch, "E1025", {"start": v(-5.65, -2.64) * mm, "end": v(-5.68, -2.65) * mm});
            skLineSegment(sketch, "E1026", {"start": v(-5.68, -2.65) * mm, "end": v(-5.74, -2.67) * mm});
            skLineSegment(sketch, "E1027", {"start": v(-5.74, -2.67) * mm, "end": v(-5.8, -2.68) * mm});
            skLineSegment(sketch, "E1028", {"start": v(-5.8, -2.68) * mm, "end": v(-5.89, -2.7) * mm});
            skLineSegment(sketch, "E1029", {"start": v(-5.89, -2.7) * mm, "end": v(-5.99, -2.7) * mm});
            skLineSegment(sketch, "E1030", {"start": v(-5.99, -2.7) * mm, "end": v(-6.1, -2.71) * mm});
            skLineSegment(sketch, "E1031", {"start": v(-6.1, -2.71) * mm, "end": v(-6.24, -2.71) * mm});
            skLineSegment(sketch, "E1032", {"start": v(-6.24, -2.71) * mm, "end": v(-6.38, -2.7) * mm});
            skLineSegment(sketch, "E1033", {"start": v(-6.38, -2.7) * mm, "end": v(-6.54, -2.7) * mm});
            skLineSegment(sketch, "E1034", {"start": v(-6.54, -2.7) * mm, "end": v(-6.7, -2.67) * mm});
            skArc(sketch, "E1035", {"start": v(-6.7, -2.67) * mm, "mid": v(-6.8, -2.36) * mm, "end": v(-6.9, -2.04) * mm});
            skLineSegment(sketch, "E1036", {"start": v(-6.9, -2.04) * mm, "end": v(-6.8, -1.94) * mm});
            skLineSegment(sketch, "E1037", {"start": v(-6.8, -1.94) * mm, "end": v(-6.69, -1.83) * mm});
            skLineSegment(sketch, "E1038", {"start": v(-6.69, -1.83) * mm, "end": v(-6.57, -1.73) * mm});
            skLineSegment(sketch, "E1039", {"start": v(-6.57, -1.73) * mm, "end": v(-6.47, -1.65) * mm});
            skLineSegment(sketch, "E1040", {"start": v(-6.47, -1.65) * mm, "end": v(-6.37, -1.58) * mm});
            skLineSegment(sketch, "E1041", {"start": v(-6.37, -1.58) * mm, "end": v(-6.29, -1.53) * mm});
            skLineSegment(sketch, "E1042", {"start": v(-6.29, -1.53) * mm, "end": v(-6.21, -1.49) * mm});
            skLineSegment(sketch, "E1043", {"start": v(-6.21, -1.49) * mm, "end": v(-6.15, -1.46) * mm});
            skLineSegment(sketch, "E1044", {"start": v(-6.15, -1.46) * mm, "end": v(-6.1, -1.44) * mm});
            skLineSegment(sketch, "E1045", {"start": v(-6.1, -1.44) * mm, "end": v(-6.06, -1.42) * mm});
            skLineSegment(sketch, "E1046", {"start": v(-6.06, -1.42) * mm, "end": v(-6.04, -1.42) * mm});
            skLineSegment(sketch, "E1047", {"start": v(-6.04, -1.42) * mm, "end": v(-6.04, -1.42) * mm});
            skLineSegment(sketch, "E1048", {"start": v(-6.04, -1.42) * mm, "end": v(-5.33, -1.25) * mm});
            skArc(sketch, "E1049", {"start": v(-5.33, -1.25) * mm, "mid": v(-5.42, -0.75) * mm, "end": v(-5.47, -0.25) * mm});
            skLineSegment(sketch, "E1050", {"start": v(-5.47, -0.25) * mm, "end": v(-6.19, -0.28) * mm});
            skLineSegment(sketch, "E1051", {"start": v(-6.19, -0.28) * mm, "end": v(-6.2, -0.28) * mm});
            skLineSegment(sketch, "E1052", {"start": v(-6.2, -0.28) * mm, "end": v(-6.22, -0.28) * mm});
            skLineSegment(sketch, "E1053", {"start": v(-6.22, -0.28) * mm, "end": v(-6.26, -0.28) * mm});
            skLineSegment(sketch, "E1054", {"start": v(-6.26, -0.28) * mm, "end": v(-6.31, -0.27) * mm});
            skLineSegment(sketch, "E1055", {"start": v(-6.31, -0.27) * mm, "end": v(-6.38, -0.26) * mm});
            skLineSegment(sketch, "E1056", {"start": v(-6.38, -0.26) * mm, "end": v(-6.46, -0.24) * mm});
            skLineSegment(sketch, "E1057", {"start": v(-6.46, -0.24) * mm, "end": v(-6.56, -0.2) * mm});
            skLineSegment(sketch, "E1058", {"start": v(-6.56, -0.2) * mm, "end": v(-6.67, -0.17) * mm});
            skLineSegment(sketch, "E1059", {"start": v(-6.67, -0.17) * mm, "end": v(-6.8, -0.12) * mm});
            skLineSegment(sketch, "E1060", {"start": v(-6.8, -0.12) * mm, "end": v(-6.93, -0.06) * mm});
            skLineSegment(sketch, "E1061", {"start": v(-6.93, -0.06) * mm, "end": v(-7.07, 0.02) * mm});
            skLineSegment(sketch, "E1062", {"start": v(-7.07, 0.02) * mm, "end": v(-7.2, 0.1) * mm});
            skArc(sketch, "E1063", {"start": v(-7.2, 0.1) * mm, "mid": v(-7.19, 0.42) * mm, "end": v(-7.16, 0.75) * mm});
            skLineSegment(sketch, "E1064", {"start": v(-7.16, 0.75) * mm, "end": v(-7.02, 0.81) * mm});
            skLineSegment(sketch, "E1065", {"start": v(-7.02, 0.81) * mm, "end": v(-6.87, 0.87) * mm});
            skLineSegment(sketch, "E1066", {"start": v(-6.87, 0.87) * mm, "end": v(-6.73, 0.92) * mm});
            skLineSegment(sketch, "E1067", {"start": v(-6.73, 0.92) * mm, "end": v(-6.6, 0.95) * mm});
            skLineSegment(sketch, "E1068", {"start": v(-6.6, 0.95) * mm, "end": v(-6.49, 0.97) * mm});
            skLineSegment(sketch, "E1069", {"start": v(-6.49, 0.97) * mm, "end": v(-6.39, 1) * mm});
            skLineSegment(sketch, "E1070", {"start": v(-6.39, 1) * mm, "end": v(-6.3, 1) * mm});
            skLineSegment(sketch, "E1071", {"start": v(-6.3, 1) * mm, "end": v(-6.24, 1) * mm});
            skLineSegment(sketch, "E1072", {"start": v(-6.24, 1) * mm, "end": v(-6.18, 1) * mm});
            skLineSegment(sketch, "E1073", {"start": v(-6.18, 1) * mm, "end": v(-6.14, 1) * mm});
            skLineSegment(sketch, "E1074", {"start": v(-6.14, 1) * mm, "end": v(-6.12, 1) * mm});
            skLineSegment(sketch, "E1075", {"start": v(-6.12, 1) * mm, "end": v(-6.11, 1) * mm});
            skLineSegment(sketch, "E1076", {"start": v(-6.11, 1) * mm, "end": v(-5.4, 0.88) * mm});
            skArc(sketch, "E1077", {"start": v(-5.4, 0.88) * mm, "mid": v(-5.3, 1.38) * mm, "end": v(-5.14, 1.86) * mm});
            skLineSegment(sketch, "E1078", {"start": v(-5.14, 1.86) * mm, "end": v(-5.82, 2.1) * mm});
            skLineSegment(sketch, "E1079", {"start": v(-5.82, 2.1) * mm, "end": v(-5.83, 2.11) * mm});
            skLineSegment(sketch, "E1080", {"start": v(-5.83, 2.11) * mm, "end": v(-5.85, 2.12) * mm});
            skLineSegment(sketch, "E1081", {"start": v(-5.85, 2.12) * mm, "end": v(-5.88, 2.14) * mm});
            skLineSegment(sketch, "E1082", {"start": v(-5.88, 2.14) * mm, "end": v(-5.93, 2.17) * mm});
            skLineSegment(sketch, "E1083", {"start": v(-5.93, 2.17) * mm, "end": v(-5.99, 2.2) * mm});
            skLineSegment(sketch, "E1084", {"start": v(-5.99, 2.2) * mm, "end": v(-6.06, 2.25) * mm});
            skLineSegment(sketch, "E1085", {"start": v(-6.06, 2.25) * mm, "end": v(-6.14, 2.32) * mm});
            skLineSegment(sketch, "E1086", {"start": v(-6.14, 2.32) * mm, "end": v(-6.22, 2.4) * mm});
            skLineSegment(sketch, "E1087", {"start": v(-6.22, 2.4) * mm, "end": v(-6.32, 2.49) * mm});
            skLineSegment(sketch, "E1088", {"start": v(-6.32, 2.49) * mm, "end": v(-6.42, 2.6) * mm});
            skLineSegment(sketch, "E1089", {"start": v(-6.42, 2.6) * mm, "end": v(-6.52, 2.72) * mm});
            skLineSegment(sketch, "E1090", {"start": v(-6.52, 2.72) * mm, "end": v(-6.61, 2.84) * mm});
            skArc(sketch, "E1091", {"start": v(-6.61, 2.84) * mm, "mid": v(-6.47, 3.14) * mm, "end": v(-6.32, 3.44) * mm});
            skLineSegment(sketch, "E1092", {"start": v(-6.32, 3.44) * mm, "end": v(-6.17, 3.44) * mm});
            skLineSegment(sketch, "E1093", {"start": v(-6.17, 3.44) * mm, "end": v(-6, 3.43) * mm});
            skLineSegment(sketch, "E1094", {"start": v(-6, 3.43) * mm, "end": v(-5.86, 3.42) * mm});
            skLineSegment(sketch, "E1095", {"start": v(-5.86, 3.42) * mm, "end": v(-5.73, 3.4) * mm});
            skLineSegment(sketch, "E1096", {"start": v(-5.73, 3.4) * mm, "end": v(-5.62, 3.38) * mm});
            skLineSegment(sketch, "E1097", {"start": v(-5.62, 3.38) * mm, "end": v(-5.52, 3.36) * mm});
            skLineSegment(sketch, "E1098", {"start": v(-5.52, 3.36) * mm, "end": v(-5.44, 3.34) * mm});
            skLineSegment(sketch, "E1099", {"start": v(-5.44, 3.34) * mm, "end": v(-5.37, 3.31) * mm});
            skLineSegment(sketch, "E1100", {"start": v(-5.37, 3.31) * mm, "end": v(-5.32, 3.3) * mm});
            skLineSegment(sketch, "E1101", {"start": v(-5.32, 3.3) * mm, "end": v(-5.29, 3.28) * mm});
            skLineSegment(sketch, "E1102", {"start": v(-5.29, 3.28) * mm, "end": v(-5.26, 3.27) * mm});
            skLineSegment(sketch, "E1103", {"start": v(-5.26, 3.27) * mm, "end": v(-5.26, 3.26) * mm});
            skLineSegment(sketch, "E1104", {"start": v(-5.26, 3.26) * mm, "end": v(-4.65, 2.88) * mm});
            skArc(sketch, "E1105", {"start": v(-4.65, 2.88) * mm, "mid": v(-4.36, 3.3) * mm, "end": v(-4.03, 3.69) * mm});
            skLineSegment(sketch, "E1106", {"start": v(-4.03, 3.69) * mm, "end": v(-4.56, 4.17) * mm});
            skLineSegment(sketch, "E1107", {"start": v(-4.56, 4.17) * mm, "end": v(-4.57, 4.18) * mm});
            skLineSegment(sketch, "E1108", {"start": v(-4.57, 4.18) * mm, "end": v(-4.59, 4.2) * mm});
            skLineSegment(sketch, "E1109", {"start": v(-4.59, 4.2) * mm, "end": v(-4.61, 4.23) * mm});
            skLineSegment(sketch, "E1110", {"start": v(-4.61, 4.23) * mm, "end": v(-4.64, 4.27) * mm});
            skLineSegment(sketch, "E1111", {"start": v(-4.64, 4.27) * mm, "end": v(-4.68, 4.33) * mm});
            skLineSegment(sketch, "E1112", {"start": v(-4.68, 4.33) * mm, "end": v(-4.73, 4.4) * mm});
            skLineSegment(sketch, "E1113", {"start": v(-4.73, 4.4) * mm, "end": v(-4.78, 4.49) * mm});
            skLineSegment(sketch, "E1114", {"start": v(-4.78, 4.49) * mm, "end": v(-4.83, 4.6) * mm});
            skLineSegment(sketch, "E1115", {"start": v(-4.83, 4.6) * mm, "end": v(-4.88, 4.71) * mm});
            skLineSegment(sketch, "E1116", {"start": v(-4.88, 4.71) * mm, "end": v(-4.93, 4.85) * mm});
            skLineSegment(sketch, "E1117", {"start": v(-4.93, 4.85) * mm, "end": v(-4.98, 5) * mm});
            skLineSegment(sketch, "E1118", {"start": v(-4.98, 5) * mm, "end": v(-5.02, 5.15) * mm});
            skArc(sketch, "E1119", {"start": v(-5.02, 5.15) * mm, "mid": v(-4.77, 5.38) * mm, "end": v(-4.52, 5.6) * mm});
            skLineSegment(sketch, "E1120", {"start": v(-4.52, 5.6) * mm, "end": v(-4.38, 5.54) * mm});
            skLineSegment(sketch, "E1121", {"start": v(-4.38, 5.54) * mm, "end": v(-4.23, 5.47) * mm});
            skLineSegment(sketch, "E1122", {"start": v(-4.23, 5.47) * mm, "end": v(-4.1, 5.4) * mm});
            skLineSegment(sketch, "E1123", {"start": v(-4.1, 5.4) * mm, "end": v(-3.99, 5.34) * mm});
            skLineSegment(sketch, "E1124", {"start": v(-3.99, 5.34) * mm, "end": v(-3.89, 5.27) * mm});
            skLineSegment(sketch, "E1125", {"start": v(-3.89, 5.27) * mm, "end": v(-3.8, 5.22) * mm});
            skLineSegment(sketch, "E1126", {"start": v(-3.8, 5.22) * mm, "end": v(-3.74, 5.16) * mm});
            skLineSegment(sketch, "E1127", {"start": v(-3.74, 5.16) * mm, "end": v(-3.69, 5.12) * mm});
            skLineSegment(sketch, "E1128", {"start": v(-3.69, 5.12) * mm, "end": v(-3.65, 5.08) * mm});
            skLineSegment(sketch, "E1129", {"start": v(-3.65, 5.08) * mm, "end": v(-3.62, 5.05) * mm});
            skLineSegment(sketch, "E1130", {"start": v(-3.62, 5.05) * mm, "end": v(-3.6, 5.03) * mm});
            skLineSegment(sketch, "E1131", {"start": v(-3.6, 5.03) * mm, "end": v(-3.6, 5.03) * mm});
            skLineSegment(sketch, "E1132", {"start": v(-3.6, 5.03) * mm, "end": v(-3.18, 4.44) * mm});
            skArc(sketch, "E1133", {"start": v(-3.18, 4.44) * mm, "mid": v(-2.76, 4.71) * mm, "end": v(-2.3, 4.95) * mm});
            skLineSegment(sketch, "E1134", {"start": v(-2.3, 4.95) * mm, "end": v(-2.61, 5.6) * mm});
            skLineSegment(sketch, "E1135", {"start": v(-2.61, 5.6) * mm, "end": v(-2.62, 5.61) * mm});
            skLineSegment(sketch, "E1136", {"start": v(-2.62, 5.61) * mm, "end": v(-2.63, 5.63) * mm});
            skLineSegment(sketch, "E1137", {"start": v(-2.63, 5.63) * mm, "end": v(-2.64, 5.67) * mm});
            skLineSegment(sketch, "E1138", {"start": v(-2.64, 5.67) * mm, "end": v(-2.65, 5.72) * mm});
            skLineSegment(sketch, "E1139", {"start": v(-2.65, 5.72) * mm, "end": v(-2.67, 5.79) * mm});
            skLineSegment(sketch, "E1140", {"start": v(-2.67, 5.79) * mm, "end": v(-2.68, 5.87) * mm});
            skLineSegment(sketch, "E1141", {"start": v(-2.68, 5.87) * mm, "end": v(-2.7, 5.97) * mm});
            skLineSegment(sketch, "E1142", {"start": v(-2.7, 5.97) * mm, "end": v(-2.7, 6.09) * mm});
            skLineSegment(sketch, "E1143", {"start": v(-2.7, 6.09) * mm, "end": v(-2.7, 6.22) * mm});
            skLineSegment(sketch, "E1144", {"start": v(-2.7, 6.22) * mm, "end": v(-2.7, 6.37) * mm});
            skLineSegment(sketch, "E1145", {"start": v(-2.7, 6.37) * mm, "end": v(-2.68, 6.53) * mm});
            skLineSegment(sketch, "E1146", {"start": v(-2.68, 6.53) * mm, "end": v(-2.66, 6.68) * mm});
            skArc(sketch, "E1147", {"start": v(-2.66, 6.68) * mm, "mid": v(-2.35, 6.8) * mm, "end": v(-2.03, 6.9) * mm});
            skLineSegment(sketch, "E1148", {"start": v(-2.03, 6.9) * mm, "end": v(-1.92, 6.8) * mm});
            skLineSegment(sketch, "E1149", {"start": v(-1.92, 6.8) * mm, "end": v(-1.81, 6.67) * mm});
            skLineSegment(sketch, "E1150", {"start": v(-1.81, 6.67) * mm, "end": v(-1.71, 6.56) * mm});
            skLineSegment(sketch, "E1151", {"start": v(-1.71, 6.56) * mm, "end": v(-1.63, 6.46) * mm});
            skLineSegment(sketch, "E1152", {"start": v(-1.63, 6.46) * mm, "end": v(-1.57, 6.36) * mm});
            skLineSegment(sketch, "E1153", {"start": v(-1.57, 6.36) * mm, "end": v(-1.52, 6.27) * mm});
            skLineSegment(sketch, "E1154", {"start": v(-1.52, 6.27) * mm, "end": v(-1.47, 6.2) * mm});
            skLineSegment(sketch, "E1155", {"start": v(-1.47, 6.2) * mm, "end": v(-1.44, 6.14) * mm});
            skLineSegment(sketch, "E1156", {"start": v(-1.44, 6.14) * mm, "end": v(-1.42, 6.09) * mm});
            skLineSegment(sketch, "E1157", {"start": v(-1.42, 6.09) * mm, "end": v(-1.4, 6.05) * mm});
            skLineSegment(sketch, "E1158", {"start": v(-1.4, 6.05) * mm, "end": v(-1.4, 6.03) * mm});
            skLineSegment(sketch, "E1159", {"start": v(-1.4, 6.03) * mm, "end": v(-1.4, 6.02) * mm});
            skLineSegment(sketch, "E1160", {"start": v(-1.4, 6.02) * mm, "end": v(-1.24, 5.32) * mm});
            skArc(sketch, "E1161", {"start": v(-1.24, 5.32) * mm, "mid": v(-0.74, 5.4) * mm, "end": v(-0.23, 5.45) * mm});
            skLineSegment(sketch, "E1162", {"start": v(-0.23, 5.45) * mm, "end": v(-0.27, 6.18) * mm});
            skLineSegment(sketch, "E1163", {"start": v(-0.27, 6.18) * mm, "end": v(-0.27, 6.18) * mm});
            skLineSegment(sketch, "E1164", {"start": v(-0.27, 6.18) * mm, "end": v(-0.26, 6.2) * mm});
            skLineSegment(sketch, "E1165", {"start": v(-0.26, 6.2) * mm, "end": v(-0.26, 6.25) * mm});
            skLineSegment(sketch, "E1166", {"start": v(-0.26, 6.25) * mm, "end": v(-0.25, 6.3) * mm});
            skLineSegment(sketch, "E1167", {"start": v(-0.25, 6.3) * mm, "end": v(-0.24, 6.37) * mm});
            skLineSegment(sketch, "E1168", {"start": v(-0.24, 6.37) * mm, "end": v(-0.22, 6.45) * mm});
            skLineSegment(sketch, "E1169", {"start": v(-0.22, 6.45) * mm, "end": v(-0.2, 6.55) * mm});
            skLineSegment(sketch, "E1170", {"start": v(-0.2, 6.55) * mm, "end": v(-0.16, 6.66) * mm});
            skLineSegment(sketch, "E1171", {"start": v(-0.16, 6.66) * mm, "end": v(-0.1, 6.78) * mm});
            skLineSegment(sketch, "E1172", {"start": v(-0.1, 6.78) * mm, "end": v(-0.05, 6.91) * mm});
            skLineSegment(sketch, "E1173", {"start": v(-0.05, 6.91) * mm, "end": v(0.03, 7.06) * mm});
            skLineSegment(sketch, "E1174", {"start": v(0.03, 7.06) * mm, "end": v(0.1, 7.18) * mm});
            skArc(sketch, "E1175", {"start": v(0.1, 7.18) * mm, "mid": v(0.44, 7.17) * mm, "end": v(0.77, 7.14) * mm});
            skLineSegment(sketch, "E1176", {"start": v(0.77, 7.14) * mm, "end": v(0.83, 7) * mm});
            skLineSegment(sketch, "E1177", {"start": v(0.83, 7) * mm, "end": v(0.89, 6.86) * mm});
            skLineSegment(sketch, "E1178", {"start": v(0.89, 6.86) * mm, "end": v(0.93, 6.72) * mm});
            skLineSegment(sketch, "E1179", {"start": v(0.93, 6.72) * mm, "end": v(0.97, 6.59) * mm});
            skLineSegment(sketch, "E1180", {"start": v(0.97, 6.59) * mm, "end": v(0.99, 6.48) * mm});
            skLineSegment(sketch, "E1181", {"start": v(0.99, 6.48) * mm, "end": v(1, 6.38) * mm});
            skLineSegment(sketch, "E1182", {"start": v(1, 6.38) * mm, "end": v(1.02, 6.3) * mm});
            skLineSegment(sketch, "E1183", {"start": v(1.02, 6.3) * mm, "end": v(1.02, 6.22) * mm});
            skLineSegment(sketch, "E1184", {"start": v(1.02, 6.22) * mm, "end": v(1.02, 6.17) * mm});
            skLineSegment(sketch, "E1185", {"start": v(1.02, 6.17) * mm, "end": v(1.02, 6.13) * mm});
            skLineSegment(sketch, "E1186", {"start": v(1.02, 6.13) * mm, "end": v(1.02, 6.1) * mm});
            skLineSegment(sketch, "E1187", {"start": v(1.02, 6.1) * mm, "end": v(1.02, 6.1) * mm});
            skLineSegment(sketch, "E1188", {"start": v(1.02, 6.1) * mm, "end": v(0.9, 5.39) * mm});
            skArc(sketch, "E1189", {"start": v(0.9, 5.39) * mm, "mid": v(1.4, 5.28) * mm, "end": v(1.88, 5.13) * mm});
            skLineSegment(sketch, "E1190", {"start": v(1.88, 5.13) * mm, "end": v(2.12, 5.8) * mm});
            skLineSegment(sketch, "E1191", {"start": v(2.12, 5.8) * mm, "end": v(2.13, 5.81) * mm});
            skLineSegment(sketch, "E1192", {"start": v(2.13, 5.81) * mm, "end": v(2.14, 5.83) * mm});
            skLineSegment(sketch, "E1193", {"start": v(2.14, 5.83) * mm, "end": v(2.15, 5.87) * mm});
            skLineSegment(sketch, "E1194", {"start": v(2.15, 5.87) * mm, "end": v(2.18, 5.92) * mm});
            skLineSegment(sketch, "E1195", {"start": v(2.18, 5.92) * mm, "end": v(2.22, 5.97) * mm});
            skLineSegment(sketch, "E1196", {"start": v(2.22, 5.97) * mm, "end": v(2.27, 6.04) * mm});
            skLineSegment(sketch, "E1197", {"start": v(2.27, 6.04) * mm, "end": v(2.33, 6.12) * mm});
            skLineSegment(sketch, "E1198", {"start": v(2.33, 6.12) * mm, "end": v(2.4, 6.2) * mm});
            skLineSegment(sketch, "E1199", {"start": v(2.4, 6.2) * mm, "end": v(2.5, 6.3) * mm});
            skLineSegment(sketch, "E1200", {"start": v(2.5, 6.3) * mm, "end": v(2.6, 6.4) * mm});
            skLineSegment(sketch, "E1201", {"start": v(2.6, 6.4) * mm, "end": v(2.73, 6.5) * mm});
            skLineSegment(sketch, "E1202", {"start": v(2.73, 6.5) * mm, "end": v(2.85, 6.6) * mm});
            skArc(sketch, "E1203", {"start": v(2.85, 6.6) * mm, "mid": v(3.16, 6.46) * mm, "end": v(3.45, 6.3) * mm});
            skLineSegment(sketch, "E1204", {"start": v(3.45, 6.3) * mm, "end": v(3.45, 6.16) * mm});
            skLineSegment(sketch, "E1205", {"start": v(3.45, 6.16) * mm, "end": v(3.45, 6) * mm});
            skLineSegment(sketch, "E1206", {"start": v(3.45, 6) * mm, "end": v(3.44, 5.85) * mm});
            skLineSegment(sketch, "E1207", {"start": v(3.44, 5.85) * mm, "end": v(3.42, 5.72) * mm});
            skLineSegment(sketch, "E1208", {"start": v(3.42, 5.72) * mm, "end": v(3.4, 5.6) * mm});
            skLineSegment(sketch, "E1209", {"start": v(3.4, 5.6) * mm, "end": v(3.37, 5.5) * mm});
            skLineSegment(sketch, "E1210", {"start": v(3.37, 5.5) * mm, "end": v(3.35, 5.42) * mm});
            skLineSegment(sketch, "E1211", {"start": v(3.35, 5.42) * mm, "end": v(3.33, 5.36) * mm});
            skLineSegment(sketch, "E1212", {"start": v(3.33, 5.36) * mm, "end": v(3.3, 5.3) * mm});
            skLineSegment(sketch, "E1213", {"start": v(3.3, 5.3) * mm, "end": v(3.3, 5.27) * mm});
            skLineSegment(sketch, "E1214", {"start": v(3.3, 5.27) * mm, "end": v(3.28, 5.25) * mm});
            skLineSegment(sketch, "E1215", {"start": v(3.28, 5.25) * mm, "end": v(3.28, 5.24) * mm});
            skLineSegment(sketch, "E1216", {"start": v(3.28, 5.24) * mm, "end": v(2.9, 4.63) * mm});
            skArc(sketch, "E1217", {"start": v(2.9, 4.63) * mm, "mid": v(3.31, 4.34) * mm, "end": v(3.7, 4.02) * mm});
            skCircle(sketch, "E1218", {"center": v(0, -0.01) * mm, "radius": 1.5 * mm});
            skSolve(sketch);
        }
        {
            var Q0;
            Q0=makeQuery(id+"F0.imprint","IMPRINT",FACE,{"disambiguationData":[TD([[makeQuery(id+"F0.imprint","IMPRINT",EDGE,{"derivedFrom":sQuery(id+"F0.wireOp",EDGE,"E0")}),-1.0]])]});
            extrude(context, id + "F1", {"entities" : qUnion([Q0]), "depth" : 5 * mm});
        }
    });
